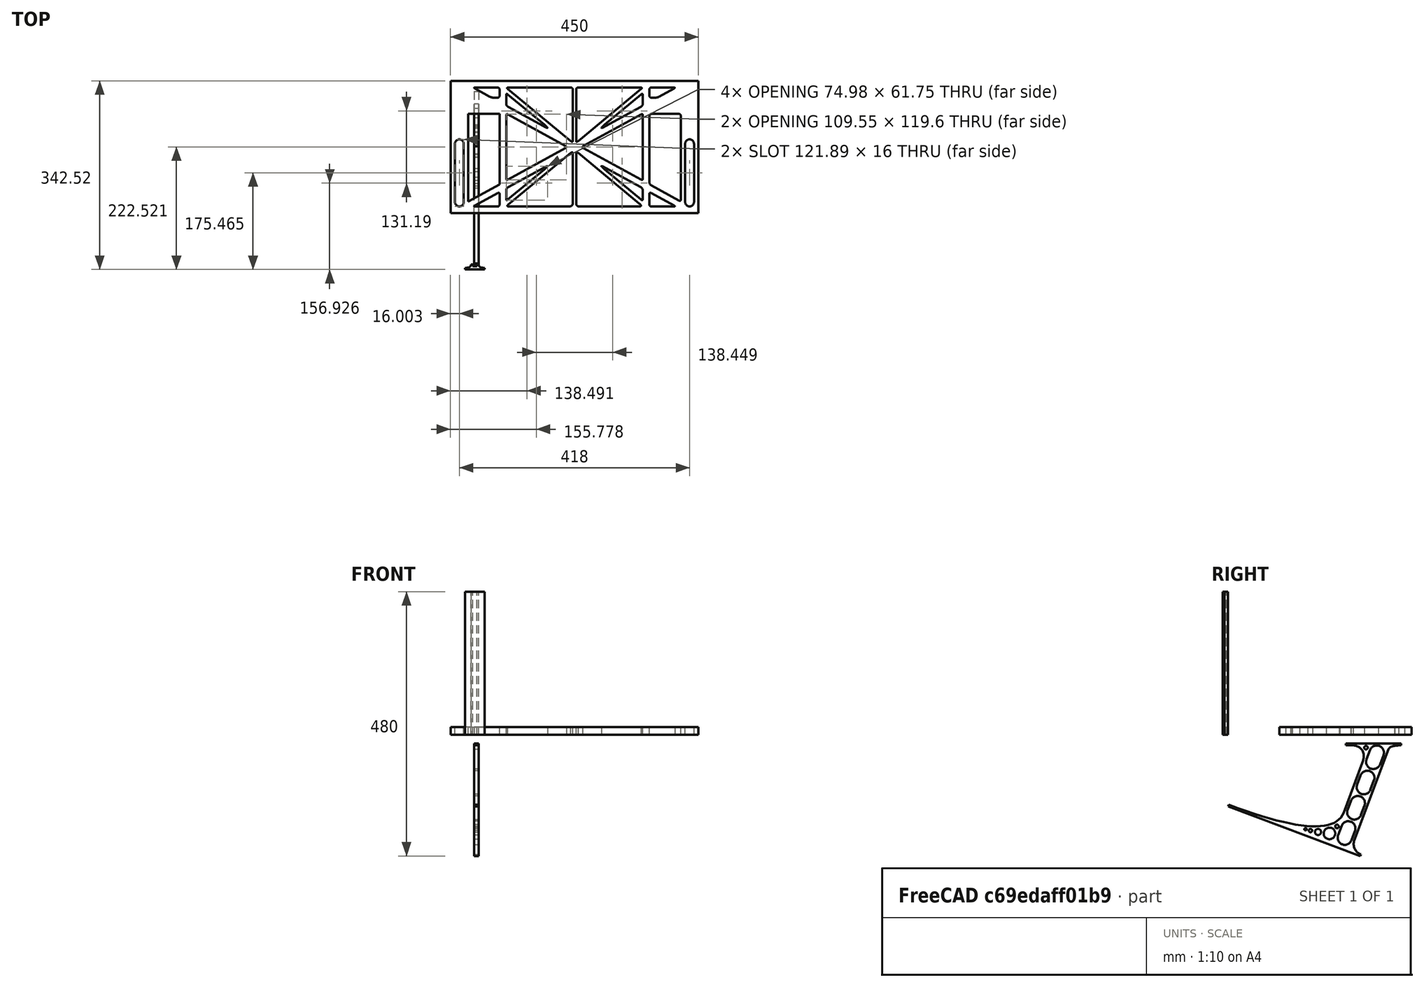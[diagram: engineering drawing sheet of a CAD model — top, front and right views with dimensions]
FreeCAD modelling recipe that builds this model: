
FCSTD DOCUMENT  (FreeCAD 0.19R0.19.2)
Label: laptopStand148FCStd
License: All rights reserved
LicenseURL: http://en.wikipedia.org/wiki/All_rights_reserved
objects: Sketcher::SketchObject×4, Part::Extrusion×3
note: 7 computed .brp shape members not serialized (recipe doc carries the construction recipe); baked Part::Feature solids carry a one-line shape summary decoded from their .brp

FEATURE [Sketcher::SketchObject] Sketch
  FullyConstrained = false
  sketch-geometry (349):
    g0: LineSegment StartX=-10.9272 StartY=-82.7794 StartZ=0 EndX=46.0728 EndY=-51.4823 EndZ=0
    g1: LineSegment StartX=-10.9272 StartY=76.4095 StartZ=0 EndX=-10.9272 EndY=-82.7794 EndZ=0
    g2: LineSegment StartX=46.0728 StartY=76.4095 StartZ=0 EndX=46.0728 EndY=-51.4823 EndZ=0
    g3: LineSegment StartX=-42.9272 StartY=136.221 StartZ=0 EndX=-42.9272 EndY=-103.779 EndZ=0
    g4: LineSegment StartX=407.073 StartY=136.221 StartZ=0 EndX=407.073 EndY=-103.779 EndZ=0
    g5: ArcOfCircle CenterX=-26.9272 CenterY=-83.7794 CenterZ=0 NormalX=0 NormalY=0 NormalZ=1 AngleXU=0 Radius=8 StartAngle=3.14159 EndAngle=6.28319
    g6: ArcOfCircle CenterX=391.073 CenterY=22.1087 CenterZ=0 NormalX=0 NormalY=0 NormalZ=1 AngleXU=0 Radius=8 StartAngle=-4.4e-15 EndAngle=3.14159
    g7: LineSegment StartX=399.073 StartY=22.1087 StartZ=0 EndX=399.073 EndY=-83.7794 EndZ=0
    g8: LineSegment StartX=383.073 StartY=22.1087 StartZ=0 EndX=383.073 EndY=-83.7794 EndZ=0
    g9: ArcOfCircle CenterX=391.073 CenterY=-83.7794 CenterZ=0 NormalX=0 NormalY=0 NormalZ=1 AngleXU=0 Radius=8 StartAngle=3.14159 EndAngle=6.28319
    g10: Circle CenterX=175.022 CenterY=27.0628 CenterZ=0 NormalX=0 NormalY=0 NormalZ=1 AngleXU=0 Radius=1
    g11: Circle CenterX=179.022 CenterY=24.8665 CenterZ=0 NormalX=0 NormalY=0 NormalZ=1 AngleXU=0 Radius=1
    g12: Circle CenterX=179.022 CenterY=27.0628 CenterZ=0 NormalX=0 NormalY=0 NormalZ=1 AngleXU=0 Radius=1
    g13: BSplineCurve PolesCount=3 KnotsCount=2 Degree=2 IsPeriodic=0
    g14: GeomPoint X=175.022 Y=27.0628 Z=0
    g15: GeomPoint X=179.022 Y=27.0628 Z=0
    g16: Circle CenterX=189.124 CenterY=27.0628 CenterZ=0 NormalX=0 NormalY=0 NormalZ=1 AngleXU=0 Radius=1
    g17: Circle CenterX=185.124 CenterY=24.8665 CenterZ=0 NormalX=0 NormalY=0 NormalZ=1 AngleXU=0 Radius=1
    g18: Circle CenterX=185.124 CenterY=27.0628 CenterZ=0 NormalX=0 NormalY=0 NormalZ=1 AngleXU=0 Radius=1
    g19: BSplineCurve PolesCount=3 KnotsCount=2 Degree=2 IsPeriodic=0
    g20: GeomPoint X=189.124 Y=27.0628 Z=0
    g21: GeomPoint X=185.124 Y=27.0628 Z=0
    g22: Circle CenterX=175.022 CenterY=5.37834 CenterZ=0 NormalX=0 NormalY=0 NormalZ=1 AngleXU=0 Radius=1
    g23: Circle CenterX=179.022 CenterY=7.57463 CenterZ=0 NormalX=0 NormalY=0 NormalZ=1 AngleXU=0 Radius=1
    g24: Circle CenterX=179.022 CenterY=5.34704 CenterZ=0 NormalX=0 NormalY=0 NormalZ=1 AngleXU=0 Radius=1
    g25: BSplineCurve PolesCount=3 KnotsCount=2 Degree=2 IsPeriodic=0
    g26: GeomPoint X=175.022 Y=5.37834 Z=0
    g27: GeomPoint X=179.022 Y=5.34704 Z=0
    g28: Circle CenterX=189.124 CenterY=5.37834 CenterZ=0 NormalX=0 NormalY=0 NormalZ=1 AngleXU=0 Radius=1
    g29: Circle CenterX=185.124 CenterY=7.57463 CenterZ=0 NormalX=0 NormalY=0 NormalZ=1 AngleXU=0 Radius=1
    g30: Circle CenterX=185.124 CenterY=5.34704 CenterZ=0 NormalX=0 NormalY=0 NormalZ=1 AngleXU=0 Radius=1
    g31: BSplineCurve PolesCount=3 KnotsCount=2 Degree=2 IsPeriodic=0
    g32: GeomPoint X=189.124 Y=5.37834 Z=0
    g33: GeomPoint X=185.124 Y=5.34704 Z=0
    g34: Circle CenterX=165.871 CenterY=18.1458 CenterZ=0 NormalX=0 NormalY=0 NormalZ=1 AngleXU=0 Radius=1
    g35: Circle CenterX=169.377 CenterY=16.2206 CenterZ=0 NormalX=0 NormalY=0 NormalZ=1 AngleXU=0 Radius=1
    g36: Circle CenterX=165.871 CenterY=14.2954 CenterZ=0 NormalX=0 NormalY=0 NormalZ=1 AngleXU=0 Radius=1
    g37: BSplineCurve PolesCount=3 KnotsCount=2 Degree=2 IsPeriodic=0
    g38: GeomPoint X=165.871 Y=18.1458 Z=0
    g39: GeomPoint X=165.871 Y=14.2954 Z=0
    g40: Circle CenterX=198.275 CenterY=18.1458 CenterZ=0 NormalX=0 NormalY=0 NormalZ=1 AngleXU=0 Radius=1
    g41: Circle CenterX=194.768 CenterY=16.2206 CenterZ=0 NormalX=0 NormalY=0 NormalZ=1 AngleXU=0 Radius=1
    g42: Circle CenterX=198.275 CenterY=14.2954 CenterZ=0 NormalX=0 NormalY=0 NormalZ=1 AngleXU=0 Radius=1
    g43: BSplineCurve PolesCount=3 KnotsCount=2 Degree=2 IsPeriodic=0
    g44: GeomPoint X=198.275 Y=18.1458 Z=0
    g45: GeomPoint X=198.275 Y=14.2954 Z=0
    g46: LineSegment StartX=407.073 StartY=-103.779 StartZ=0 EndX=-42.9272 EndY=-103.779 EndZ=0
    g47: LineSegment StartX=407.073 StartY=136.221 StartZ=0 EndX=-42.9272 EndY=136.221 EndZ=0
    g48: LineSegment StartX=46.0728 StartY=76.4095 StartZ=0 EndX=-10.9272 EndY=76.4095 EndZ=0
    g49: Circle CenterX=125.607 CenterY=54.1951 CenterZ=0 NormalX=0 NormalY=0 NormalZ=1 AngleXU=0 Radius=1
    g50: Circle CenterX=139.632 CenterY=46.4944 CenterZ=0 NormalX=0 NormalY=0 NormalZ=1 AngleXU=0 Radius=1
    g51: Circle CenterX=127.326 CenterY=56.7187 CenterZ=0 NormalX=0 NormalY=0 NormalZ=1 AngleXU=0 Radius=1
    g52: BSplineCurve PolesCount=3 KnotsCount=2 Degree=2 IsPeriodic=0
    g53: GeomPoint X=125.607 Y=54.1951 Z=0
    g54: GeomPoint X=127.326 Y=56.7187 Z=0
    g55: Circle CenterX=236.821 CenterY=56.7187 CenterZ=0 NormalX=0 NormalY=0 NormalZ=1 AngleXU=0 Radius=1
    g56: Circle CenterX=224.513 CenterY=46.4944 CenterZ=0 NormalX=0 NormalY=0 NormalZ=1 AngleXU=0 Radius=1
    g57: Circle CenterX=238.538 CenterY=54.1951 CenterZ=0 NormalX=0 NormalY=0 NormalZ=1 AngleXU=0 Radius=1
    g58: BSplineCurve PolesCount=3 KnotsCount=2 Degree=2 IsPeriodic=0
    g59: GeomPoint X=236.821 Y=56.7187 Z=0
    g60: GeomPoint X=238.538 Y=54.1951 Z=0
    g61: Circle CenterX=238.538 CenterY=-21.7539 CenterZ=0 NormalX=0 NormalY=0 NormalZ=1 AngleXU=0 Radius=1
    g62: Circle CenterX=224.513 CenterY=-14.0532 CenterZ=0 NormalX=0 NormalY=0 NormalZ=1 AngleXU=0 Radius=1
    g63: Circle CenterX=236.821 CenterY=-24.2775 CenterZ=0 NormalX=0 NormalY=0 NormalZ=1 AngleXU=0 Radius=1
    g64: BSplineCurve PolesCount=3 KnotsCount=2 Degree=2 IsPeriodic=0
    g65: GeomPoint X=238.538 Y=-21.7539 Z=0
    g66: GeomPoint X=236.821 Y=-24.2775 Z=0
    g67: Circle CenterX=125.607 CenterY=-21.7539 CenterZ=0 NormalX=0 NormalY=0 NormalZ=1 AngleXU=0 Radius=1
    g68: Circle CenterX=139.632 CenterY=-14.0532 CenterZ=0 NormalX=0 NormalY=0 NormalZ=1 AngleXU=0 Radius=1
    g69: Circle CenterX=127.325 CenterY=-24.2775 CenterZ=0 NormalX=0 NormalY=0 NormalZ=1 AngleXU=0 Radius=1
    g70: BSplineCurve PolesCount=3 KnotsCount=2 Degree=2 IsPeriodic=0
    g71: GeomPoint X=125.607 Y=-21.7539 Z=0
    g72: GeomPoint X=127.325 Y=-24.2775 Z=0
    g73: Circle CenterX=302.996 CenterY=111.695 CenterZ=0 NormalX=0 NormalY=0 NormalZ=1 AngleXU=0 Radius=1
    g74: Circle CenterX=306.073 CenterY=114.251 CenterZ=0 NormalX=0 NormalY=0 NormalZ=1 AngleXU=0 Radius=1
    g75: Circle CenterX=306.073 CenterY=110.251 CenterZ=0 NormalX=0 NormalY=0 NormalZ=1 AngleXU=0 Radius=1
    g76: BSplineCurve PolesCount=3 KnotsCount=2 Degree=2 IsPeriodic=0
    g77: GeomPoint X=302.996 Y=111.695 Z=0
    g78: GeomPoint X=306.073 Y=110.251 Z=0
    g79: Circle CenterX=306.073 CenterY=95.2763 CenterZ=0 NormalX=0 NormalY=0 NormalZ=1 AngleXU=0 Radius=1
    g80: Circle CenterX=306.073 CenterY=91.2763 CenterZ=0 NormalX=0 NormalY=0 NormalZ=1 AngleXU=0 Radius=1
    g81: Circle CenterX=302.567 CenterY=89.3511 CenterZ=0 NormalX=0 NormalY=0 NormalZ=1 AngleXU=0 Radius=1
    g82: BSplineCurve PolesCount=3 KnotsCount=2 Degree=2 IsPeriodic=0
    g83: GeomPoint X=306.073 Y=95.2763 Z=0
    g84: GeomPoint X=302.567 Y=89.3511 Z=0
    g85: LineSegment StartX=306.073 StartY=110.251 StartZ=0 EndX=306.073 EndY=95.2763 EndZ=0
    g86: LineSegment StartX=302.996 StartY=111.695 StartZ=0 EndX=236.821 EndY=56.7187 EndZ=0
    g87: LineSegment StartX=238.538 StartY=54.1951 StartZ=0 EndX=302.567 EndY=89.3511 EndZ=0
    g88: Circle CenterX=61.1496 CenterY=111.695 CenterZ=0 NormalX=0 NormalY=0 NormalZ=1 AngleXU=0 Radius=1
    g89: Circle CenterX=58.0728 CenterY=114.251 CenterZ=0 NormalX=0 NormalY=0 NormalZ=1 AngleXU=0 Radius=1
    g90: Circle CenterX=58.0728 CenterY=110.251 CenterZ=0 NormalX=0 NormalY=0 NormalZ=1 AngleXU=0 Radius=1
    g91: BSplineCurve PolesCount=3 KnotsCount=2 Degree=2 IsPeriodic=0
    g92: GeomPoint X=61.1496 Y=111.695 Z=0
    g93: GeomPoint X=58.0728 Y=110.251 Z=0
    g94: Circle CenterX=61.5791 CenterY=89.3511 CenterZ=0 NormalX=0 NormalY=0 NormalZ=1 AngleXU=0 Radius=1
    g95: Circle CenterX=58.0728 CenterY=91.2763 CenterZ=0 NormalX=0 NormalY=0 NormalZ=1 AngleXU=0 Radius=1
    g96: Circle CenterX=58.0728 CenterY=95.2763 CenterZ=0 NormalX=0 NormalY=0 NormalZ=1 AngleXU=0 Radius=1
    g97: BSplineCurve PolesCount=3 KnotsCount=2 Degree=2 IsPeriodic=0
    g98: GeomPoint X=61.5791 Y=89.3511 Z=0
    g99: GeomPoint X=58.0728 Y=95.2763 Z=0
    g100: LineSegment StartX=58.0728 StartY=110.251 StartZ=0 EndX=58.0728 EndY=95.2763 EndZ=0
    g101: LineSegment StartX=61.1496 StartY=111.695 StartZ=0 EndX=127.326 EndY=56.7187 EndZ=0
    g102: LineSegment StartX=125.607 StartY=54.1951 StartZ=0 EndX=61.5791 EndY=89.3511 EndZ=0
    g103: Circle CenterX=61.5791 CenterY=-56.9099 CenterZ=0 NormalX=0 NormalY=0 NormalZ=1 AngleXU=0 Radius=1
    g104: Circle CenterX=58.0728 CenterY=-58.8351 CenterZ=0 NormalX=0 NormalY=0 NormalZ=1 AngleXU=0 Radius=1
    g105: Circle CenterX=58.0728 CenterY=-62.8351 CenterZ=0 NormalX=0 NormalY=0 NormalZ=1 AngleXU=0 Radius=1
    g106: BSplineCurve PolesCount=3 KnotsCount=2 Degree=2 IsPeriodic=0
    g107: GeomPoint X=61.5791 Y=-56.9099 Z=0
    g108: GeomPoint X=58.0728 Y=-62.8351 Z=0
    g109: Circle CenterX=58.0728 CenterY=-77.8102 CenterZ=0 NormalX=0 NormalY=0 NormalZ=1 AngleXU=0 Radius=1
    g110: Circle CenterX=58.0728 CenterY=-81.8102 CenterZ=0 NormalX=0 NormalY=0 NormalZ=1 AngleXU=0 Radius=1
    g111: Circle CenterX=61.1496 CenterY=-79.2541 CenterZ=0 NormalX=0 NormalY=0 NormalZ=1 AngleXU=0 Radius=1
    g112: BSplineCurve PolesCount=3 KnotsCount=2 Degree=2 IsPeriodic=0
    g113: GeomPoint X=58.0728 Y=-77.8102 Z=0
    g114: GeomPoint X=61.1496 Y=-79.2541 Z=0
    g115: LineSegment StartX=58.0728 StartY=-62.8351 StartZ=0 EndX=58.0728 EndY=-77.8102 EndZ=0
    g116: LineSegment StartX=61.1496 StartY=-79.2541 StartZ=0 EndX=127.325 EndY=-24.2775 EndZ=0
    g117: LineSegment StartX=125.607 StartY=-21.7539 StartZ=0 EndX=61.5791 EndY=-56.9099 EndZ=0
    g118: Circle CenterX=302.567 CenterY=-56.9099 CenterZ=0 NormalX=0 NormalY=0 NormalZ=1 AngleXU=0 Radius=1
    g119: Circle CenterX=306.073 CenterY=-58.8351 CenterZ=0 NormalX=0 NormalY=0 NormalZ=1 AngleXU=0 Radius=1
    g120: Circle CenterX=306.073 CenterY=-62.8351 CenterZ=0 NormalX=0 NormalY=0 NormalZ=1 AngleXU=0 Radius=1
    g121: BSplineCurve PolesCount=3 KnotsCount=2 Degree=2 IsPeriodic=0
    g122: GeomPoint X=302.567 Y=-56.9099 Z=0
    g123: GeomPoint X=306.073 Y=-62.8351 Z=0
    g124: Circle CenterX=302.996 CenterY=-79.2541 CenterZ=0 NormalX=0 NormalY=0 NormalZ=1 AngleXU=0 Radius=1
    g125: Circle CenterX=306.073 CenterY=-81.8102 CenterZ=0 NormalX=0 NormalY=0 NormalZ=1 AngleXU=0 Radius=1
    g126: Circle CenterX=306.073 CenterY=-77.8102 CenterZ=0 NormalX=0 NormalY=0 NormalZ=1 AngleXU=0 Radius=1
    g127: BSplineCurve PolesCount=3 KnotsCount=2 Degree=2 IsPeriodic=0
    g128: GeomPoint X=302.996 Y=-79.2541 Z=0
    g129: GeomPoint X=306.073 Y=-77.8102 Z=0
    g130: LineSegment StartX=306.073 StartY=-62.8351 StartZ=0 EndX=306.073 EndY=-77.8102 EndZ=0
    g131: LineSegment StartX=302.996 StartY=-79.2541 StartZ=0 EndX=236.821 EndY=-24.2775 EndZ=0
    g132: LineSegment StartX=238.538 StartY=-21.7539 StartZ=0 EndX=302.567 EndY=-56.9099 EndZ=0
    g133: Circle CenterX=61.6457 CenterY=-88.8112 CenterZ=0 NormalX=0 NormalY=0 NormalZ=1 AngleXU=0 Radius=1
    g134: Circle CenterX=58.0728 CenterY=-91.7794 CenterZ=0 NormalX=0 NormalY=0 NormalZ=1 AngleXU=0 Radius=1
    g135: Circle CenterX=63.9135 CenterY=-91.7794 CenterZ=0 NormalX=0 NormalY=0 NormalZ=1 AngleXU=0 Radius=1
    g136: BSplineCurve PolesCount=3 KnotsCount=2 Degree=2 IsPeriodic=0
    g137: GeomPoint X=61.6457 Y=-88.8112 Z=0
    g138: GeomPoint X=63.9135 Y=-91.7794 Z=0
    g139: Circle CenterX=179.022 CenterY=-85.8163 CenterZ=0 NormalX=0 NormalY=0 NormalZ=1 AngleXU=0 Radius=1
    g140: Circle CenterX=179.022 CenterY=-91.7794 CenterZ=0 NormalX=0 NormalY=0 NormalZ=1 AngleXU=0 Radius=1
    g141: Circle CenterX=171.895 CenterY=-91.7794 CenterZ=0 NormalX=0 NormalY=0 NormalZ=1 AngleXU=0 Radius=1
    g142: BSplineCurve PolesCount=3 KnotsCount=2 Degree=2 IsPeriodic=0
    g143: GeomPoint X=179.022 Y=-85.8163 Z=0
    g144: GeomPoint X=171.895 Y=-91.7794 Z=0
    g145: Circle CenterX=185.124 CenterY=-86.2028 CenterZ=0 NormalX=0 NormalY=0 NormalZ=1 AngleXU=0 Radius=1
    g146: Circle CenterX=185.124 CenterY=-91.7794 CenterZ=0 NormalX=0 NormalY=0 NormalZ=1 AngleXU=0 Radius=1
    g147: Circle CenterX=191.747 CenterY=-91.7794 CenterZ=0 NormalX=0 NormalY=0 NormalZ=1 AngleXU=0 Radius=1
    g148: BSplineCurve PolesCount=3 KnotsCount=2 Degree=2 IsPeriodic=0
    g149: GeomPoint X=185.124 Y=-86.2028 Z=0
    g150: GeomPoint X=191.747 Y=-91.7794 Z=0
    g151: Circle CenterX=299.888 CenterY=-86.6413 CenterZ=0 NormalX=0 NormalY=0 NormalZ=1 AngleXU=0 Radius=1
    g152: Circle CenterX=306.073 CenterY=-91.7794 CenterZ=0 NormalX=0 NormalY=0 NormalZ=1 AngleXU=0 Radius=1
    g153: Circle CenterX=298.776 CenterY=-91.7794 CenterZ=0 NormalX=0 NormalY=0 NormalZ=1 AngleXU=0 Radius=1
    g154: BSplineCurve PolesCount=3 KnotsCount=2 Degree=2 IsPeriodic=0
    g155: GeomPoint X=299.888 Y=-86.6413 Z=0
    g156: GeomPoint X=298.776 Y=-91.7794 Z=0
    g157: LineSegment StartX=189.124 StartY=5.37834 StartZ=0 EndX=299.888 EndY=-86.6413 EndZ=0
    g158: LineSegment StartX=298.776 StartY=-91.7794 StartZ=0 EndX=191.747 EndY=-91.7794 EndZ=0
    g159: LineSegment StartX=185.124 StartY=-86.2028 StartZ=0 EndX=185.124 EndY=5.34704 EndZ=0
    g160: LineSegment StartX=179.022 StartY=5.34704 StartZ=0 EndX=179.022 EndY=-85.8163 EndZ=0
    g161: LineSegment StartX=171.895 StartY=-91.7794 StartZ=0 EndX=63.9135 EndY=-91.7794 EndZ=0
    g162: LineSegment StartX=61.6457 StartY=-88.8112 StartZ=0 EndX=175.022 EndY=5.37834 EndZ=0
    g163: Circle CenterX=302.073 CenterY=124.221 CenterZ=0 NormalX=0 NormalY=0 NormalZ=1 AngleXU=0 Radius=1
    g164: Circle CenterX=306.073 CenterY=124.221 CenterZ=0 NormalX=0 NormalY=0 NormalZ=1 AngleXU=0 Radius=1
    g165: Circle CenterX=302.996 CenterY=121.665 CenterZ=0 NormalX=0 NormalY=0 NormalZ=1 AngleXU=0 Radius=1
    g166: BSplineCurve PolesCount=3 KnotsCount=2 Degree=2 IsPeriodic=0
    g167: GeomPoint X=302.073 Y=124.221 Z=0
    g168: GeomPoint X=302.996 Y=121.665 Z=0
    g169: Circle CenterX=189.124 CenterY=124.221 CenterZ=0 NormalX=0 NormalY=0 NormalZ=1 AngleXU=0 Radius=1
    g170: Circle CenterX=185.124 CenterY=124.221 CenterZ=0 NormalX=0 NormalY=0 NormalZ=1 AngleXU=0 Radius=1
    g171: Circle CenterX=185.124 CenterY=120.221 CenterZ=0 NormalX=0 NormalY=0 NormalZ=1 AngleXU=0 Radius=1
    g172: BSplineCurve PolesCount=3 KnotsCount=2 Degree=2 IsPeriodic=0
    g173: GeomPoint X=189.124 Y=124.221 Z=0
    g174: GeomPoint X=185.124 Y=120.221 Z=0
    g175: Circle CenterX=175.022 CenterY=124.221 CenterZ=0 NormalX=0 NormalY=0 NormalZ=1 AngleXU=0 Radius=1
    g176: Circle CenterX=179.022 CenterY=124.221 CenterZ=0 NormalX=0 NormalY=0 NormalZ=1 AngleXU=0 Radius=1
    g177: Circle CenterX=179.022 CenterY=120.221 CenterZ=0 NormalX=0 NormalY=0 NormalZ=1 AngleXU=0 Radius=1
    g178: BSplineCurve PolesCount=3 KnotsCount=2 Degree=2 IsPeriodic=0
    g179: GeomPoint X=175.022 Y=124.221 Z=0
    g180: GeomPoint X=179.022 Y=120.221 Z=0
    g181: Circle CenterX=62.0728 CenterY=124.221 CenterZ=0 NormalX=0 NormalY=0 NormalZ=1 AngleXU=0 Radius=1
    g182: Circle CenterX=58.0728 CenterY=124.221 CenterZ=0 NormalX=0 NormalY=0 NormalZ=1 AngleXU=0 Radius=1
    g183: Circle CenterX=61.1496 CenterY=121.665 CenterZ=0 NormalX=0 NormalY=0 NormalZ=1 AngleXU=0 Radius=1
    g184: BSplineCurve PolesCount=3 KnotsCount=2 Degree=2 IsPeriodic=0
    g185: GeomPoint X=62.0728 Y=124.221 Z=0
    g186: GeomPoint X=61.1496 Y=121.665 Z=0
    g187: LineSegment StartX=62.0728 StartY=124.221 StartZ=0 EndX=175.022 EndY=124.221 EndZ=0
    g188: LineSegment StartX=179.022 StartY=120.221 StartZ=0 EndX=179.022 EndY=27.0628 EndZ=0
    g189: LineSegment StartX=185.124 StartY=27.0628 StartZ=0 EndX=185.124 EndY=120.221 EndZ=0
    g190: LineSegment StartX=189.124 StartY=124.221 StartZ=0 EndX=302.073 EndY=124.221 EndZ=0
    g191: LineSegment StartX=302.996 StartY=121.665 StartZ=0 EndX=189.124 EndY=27.0628 EndZ=0
    g192: LineSegment StartX=175.022 StartY=27.0628 StartZ=0 EndX=61.1496 EndY=121.665 EndZ=0
    g193: Circle CenterX=61.5791 CenterY=75.4095 CenterZ=0 NormalX=0 NormalY=0 NormalZ=1 AngleXU=0 Radius=1
    g194: Circle CenterX=58.0728 CenterY=77.3346 CenterZ=0 NormalX=0 NormalY=0 NormalZ=1 AngleXU=0 Radius=1
    g195: Circle CenterX=58.0728 CenterY=73.3346 CenterZ=0 NormalX=0 NormalY=0 NormalZ=1 AngleXU=0 Radius=1
    g196: BSplineCurve PolesCount=3 KnotsCount=2 Degree=2 IsPeriodic=0
    g197: GeomPoint X=61.5791 Y=75.4095 Z=0
    g198: GeomPoint X=58.0728 Y=73.3346 Z=0
    g199: Circle CenterX=58.0728 CenterY=-40.8935 CenterZ=0 NormalX=0 NormalY=0 NormalZ=1 AngleXU=0 Radius=1
    g200: Circle CenterX=58.0728 CenterY=-44.8935 CenterZ=0 NormalX=0 NormalY=0 NormalZ=1 AngleXU=0 Radius=1
    g201: Circle CenterX=61.5791 CenterY=-42.9683 CenterZ=0 NormalX=0 NormalY=0 NormalZ=1 AngleXU=0 Radius=1
    g202: BSplineCurve PolesCount=3 KnotsCount=2 Degree=2 IsPeriodic=0
    g203: GeomPoint X=58.0728 Y=-40.8935 Z=0
    g204: GeomPoint X=61.5791 Y=-42.9683 Z=0
    g205: LineSegment StartX=61.5791 StartY=-42.9683 StartZ=0 EndX=165.871 EndY=14.2954 EndZ=0
    g206: LineSegment StartX=165.871 StartY=18.1458 StartZ=0 EndX=61.5791 EndY=75.4095 EndZ=0
    g207: LineSegment StartX=58.0728 StartY=73.3346 StartZ=0 EndX=58.0728 EndY=-40.8935 EndZ=0
    g208: Circle CenterX=302.567 CenterY=-42.9683 CenterZ=0 NormalX=0 NormalY=0 NormalZ=1 AngleXU=0 Radius=1
    g209: Circle CenterX=306.073 CenterY=-44.8935 CenterZ=0 NormalX=0 NormalY=0 NormalZ=1 AngleXU=0 Radius=1
    g210: Circle CenterX=306.073 CenterY=-40.8935 CenterZ=0 NormalX=0 NormalY=0 NormalZ=1 AngleXU=0 Radius=1
    g211: BSplineCurve PolesCount=3 KnotsCount=2 Degree=2 IsPeriodic=0
    g212: GeomPoint X=302.567 Y=-42.9683 Z=0
    g213: GeomPoint X=306.073 Y=-40.8935 Z=0
    g214: Circle CenterX=306.073 CenterY=73.3346 CenterZ=0 NormalX=0 NormalY=0 NormalZ=1 AngleXU=0 Radius=1
    g215: Circle CenterX=306.073 CenterY=77.3346 CenterZ=0 NormalX=0 NormalY=0 NormalZ=1 AngleXU=0 Radius=1
    g216: Circle CenterX=302.567 CenterY=75.4095 CenterZ=0 NormalX=0 NormalY=0 NormalZ=1 AngleXU=0 Radius=1
    g217: BSplineCurve PolesCount=3 KnotsCount=2 Degree=2 IsPeriodic=0
    g218: GeomPoint X=306.073 Y=73.3346 Z=0
    g219: GeomPoint X=302.567 Y=75.4095 Z=0
    g220: LineSegment StartX=302.567 StartY=-42.9683 StartZ=0 EndX=198.275 EndY=14.2954 EndZ=0
    g221: LineSegment StartX=198.275 StartY=18.1458 StartZ=0 EndX=302.567 EndY=75.4095 EndZ=0
    g222: LineSegment StartX=306.073 StartY=73.3346 StartZ=0 EndX=306.073 EndY=-40.8935 EndZ=0
    g223: LineSegment StartX=322.073 StartY=105.865 StartZ=0 EndX=328.643 EndY=105.865 EndZ=0
    g224: LineSegment StartX=318.073 StartY=120.221 StartZ=0 EndX=318.073 EndY=109.865 EndZ=0
    g225: LineSegment StartX=336.157 StartY=107.779 StartZ=0 EndX=362.567 EndY=122.294 EndZ=0
    g226: Circle CenterX=362.073 CenterY=124.221 CenterZ=0 NormalX=0 NormalY=0 NormalZ=1 AngleXU=0 Radius=1
    g227: Circle CenterX=366.073 CenterY=124.221 CenterZ=0 NormalX=0 NormalY=0 NormalZ=1 AngleXU=0 Radius=1
    g228: Circle CenterX=362.567 CenterY=122.294 CenterZ=0 NormalX=0 NormalY=0 NormalZ=1 AngleXU=0 Radius=1
    g229: BSplineCurve PolesCount=3 KnotsCount=2 Degree=2 IsPeriodic=0
    g230: GeomPoint X=362.073 Y=124.221 Z=0
    g231: GeomPoint X=362.567 Y=122.294 Z=0
    g232: Circle CenterX=322.073 CenterY=124.221 CenterZ=0 NormalX=0 NormalY=0 NormalZ=1 AngleXU=0 Radius=1
    g233: Circle CenterX=318.073 CenterY=124.221 CenterZ=0 NormalX=0 NormalY=0 NormalZ=1 AngleXU=0 Radius=1
    g234: Circle CenterX=318.073 CenterY=120.221 CenterZ=0 NormalX=0 NormalY=0 NormalZ=1 AngleXU=0 Radius=1
    g235: BSplineCurve PolesCount=3 KnotsCount=2 Degree=2 IsPeriodic=0
    g236: GeomPoint X=322.073 Y=124.221 Z=0
    g237: GeomPoint X=318.073 Y=120.221 Z=0
    g238: Circle CenterX=322.073 CenterY=105.865 CenterZ=0 NormalX=0 NormalY=0 NormalZ=1 AngleXU=0 Radius=1
    g239: Circle CenterX=318.073 CenterY=105.865 CenterZ=0 NormalX=0 NormalY=0 NormalZ=1 AngleXU=0 Radius=1
    g240: Circle CenterX=318.073 CenterY=109.865 CenterZ=0 NormalX=0 NormalY=0 NormalZ=1 AngleXU=0 Radius=1
    g241: BSplineCurve PolesCount=3 KnotsCount=2 Degree=2 IsPeriodic=0
    g242: GeomPoint X=322.073 Y=105.865 Z=0
    g243: GeomPoint X=318.073 Y=109.865 Z=0
    g244: Circle CenterX=336.157 CenterY=107.779 CenterZ=0 NormalX=0 NormalY=0 NormalZ=1 AngleXU=0 Radius=1
    g245: Circle CenterX=332.651 CenterY=105.853 CenterZ=0 NormalX=0 NormalY=0 NormalZ=1 AngleXU=0 Radius=1
    g246: Circle CenterX=328.643 CenterY=105.865 CenterZ=0 NormalX=0 NormalY=0 NormalZ=1 AngleXU=0 Radius=1
    g247: BSplineCurve PolesCount=3 KnotsCount=2 Degree=2 IsPeriodic=0
    g248: GeomPoint X=336.157 Y=107.779 Z=0
    g249: GeomPoint X=328.643 Y=105.865 Z=0
    g250: LineSegment StartX=322.073 StartY=124.221 StartZ=0 EndX=362.073 EndY=124.221 EndZ=0
    g251: Circle CenterX=371.567 CenterY=-80.8644 CenterZ=0 NormalX=0 NormalY=0 NormalZ=1 AngleXU=0 Radius=1
    g252: Circle CenterX=375.073 CenterY=-82.7896 CenterZ=0 NormalX=0 NormalY=0 NormalZ=1 AngleXU=0 Radius=1
    g253: Circle CenterX=375.073 CenterY=-78.7896 CenterZ=0 NormalX=0 NormalY=0 NormalZ=1 AngleXU=0 Radius=1
    g254: BSplineCurve PolesCount=3 KnotsCount=2 Degree=2 IsPeriodic=0
    g255: GeomPoint X=371.567 Y=-80.8644 Z=0
    g256: GeomPoint X=375.073 Y=-78.7896 Z=0
    g257: Circle CenterX=321.579 CenterY=-53.4075 CenterZ=0 NormalX=0 NormalY=0 NormalZ=1 AngleXU=0 Radius=1
    g258: Circle CenterX=318.073 CenterY=-51.4823 CenterZ=0 NormalX=0 NormalY=0 NormalZ=1 AngleXU=0 Radius=1
    g259: Circle CenterX=318.073 CenterY=-47.4805 CenterZ=0 NormalX=0 NormalY=0 NormalZ=1 AngleXU=0 Radius=1
    g260: BSplineCurve PolesCount=3 KnotsCount=2 Degree=2 IsPeriodic=0
    g261: GeomPoint X=321.579 Y=-53.4075 Z=0
    g262: GeomPoint X=318.073 Y=-47.4805 Z=0
    g263: LineSegment StartX=371.567 StartY=-80.8644 StartZ=0 EndX=321.579 EndY=-53.4075 EndZ=0
    g264: Circle CenterX=321.579 CenterY=-67.3492 CenterZ=0 NormalX=0 NormalY=0 NormalZ=1 AngleXU=0 Radius=1
    g265: Circle CenterX=318.073 CenterY=-65.424 CenterZ=0 NormalX=0 NormalY=0 NormalZ=1 AngleXU=0 Radius=1
    g266: Circle CenterX=318.073 CenterY=-69.424 CenterZ=0 NormalX=0 NormalY=0 NormalZ=1 AngleXU=0 Radius=1
    g267: BSplineCurve PolesCount=3 KnotsCount=2 Degree=2 IsPeriodic=0
    g268: GeomPoint X=321.579 Y=-67.3492 Z=0
    g269: GeomPoint X=318.073 Y=-69.424 Z=0
    g270: Circle CenterX=362.567 CenterY=-89.8542 CenterZ=0 NormalX=0 NormalY=0 NormalZ=1 AngleXU=0 Radius=1
    g271: Circle CenterX=366.073 CenterY=-91.7794 CenterZ=0 NormalX=0 NormalY=0 NormalZ=1 AngleXU=0 Radius=1
    g272: Circle CenterX=362.073 CenterY=-91.7794 CenterZ=0 NormalX=0 NormalY=0 NormalZ=1 AngleXU=0 Radius=1
    g273: BSplineCurve PolesCount=3 KnotsCount=2 Degree=2 IsPeriodic=0
    g274: GeomPoint X=362.567 Y=-89.8542 Z=0
    g275: GeomPoint X=362.073 Y=-91.7794 Z=0
    g276: Circle CenterX=322.073 CenterY=-91.7794 CenterZ=0 NormalX=0 NormalY=0 NormalZ=1 AngleXU=0 Radius=1
    g277: Circle CenterX=318.073 CenterY=-91.7794 CenterZ=0 NormalX=0 NormalY=0 NormalZ=1 AngleXU=0 Radius=1
    g278: Circle CenterX=318.073 CenterY=-87.7794 CenterZ=0 NormalX=0 NormalY=0 NormalZ=1 AngleXU=0 Radius=1
    g279: BSplineCurve PolesCount=3 KnotsCount=2 Degree=2 IsPeriodic=0
    g280: GeomPoint X=322.073 Y=-91.7794 Z=0
    g281: GeomPoint X=318.073 Y=-87.7794 Z=0
    g282: LineSegment StartX=362.567 StartY=-89.8542 StartZ=0 EndX=321.579 EndY=-67.3492 EndZ=0
    g283: LineSegment StartX=318.073 StartY=-69.424 StartZ=0 EndX=318.073 EndY=-87.7794 EndZ=0
    g284: LineSegment StartX=322.073 StartY=-91.7794 StartZ=0 EndX=362.073 EndY=-91.7794 EndZ=0
    g285: Circle CenterX=2.07281 CenterY=124.221 CenterZ=0 NormalX=0 NormalY=0 NormalZ=1 AngleXU=0 Radius=1
    g286: Circle CenterX=1.57905 CenterY=122.295 CenterZ=0 NormalX=0 NormalY=0 NormalZ=1 AngleXU=0 Radius=1
    g287: BSplineCurve PolesCount=3 KnotsCount=2 Degree=2 IsPeriodic=0
    g288: GeomPoint X=2.07281 Y=124.221 Z=0
    g289: GeomPoint X=1.57905 Y=122.295 Z=0
    g290: Circle CenterX=42.0728 CenterY=124.221 CenterZ=0 NormalX=0 NormalY=0 NormalZ=1 AngleXU=0 Radius=1
    g291: Circle CenterX=46.0728 CenterY=124.221 CenterZ=0 NormalX=0 NormalY=0 NormalZ=1 AngleXU=0 Radius=1
    g292: Circle CenterX=46.0728 CenterY=120.221 CenterZ=0 NormalX=0 NormalY=0 NormalZ=1 AngleXU=0 Radius=1
    g293: BSplineCurve PolesCount=3 KnotsCount=2 Degree=2 IsPeriodic=0
    g294: GeomPoint X=42.0728 Y=124.221 Z=0
    g295: GeomPoint X=46.0728 Y=120.221 Z=0
    g296: Circle CenterX=46.0728 CenterY=109.865 CenterZ=0 NormalX=0 NormalY=0 NormalZ=1 AngleXU=0 Radius=1
    g297: Circle CenterX=46.0728 CenterY=105.865 CenterZ=0 NormalX=0 NormalY=0 NormalZ=1 AngleXU=0 Radius=1
    g298: Circle CenterX=42.0728 CenterY=105.865 CenterZ=0 NormalX=0 NormalY=0 NormalZ=1 AngleXU=0 Radius=1
    g299: BSplineCurve PolesCount=3 KnotsCount=2 Degree=2 IsPeriodic=0
    g300: GeomPoint X=46.0728 Y=109.865 Z=0
    g301: GeomPoint X=42.0728 Y=105.865 Z=0
    g302: Circle CenterX=35.5028 CenterY=105.865 CenterZ=0 NormalX=0 NormalY=0 NormalZ=1 AngleXU=0 Radius=1
    g303: Circle CenterX=31.5028 CenterY=105.865 CenterZ=0 NormalX=0 NormalY=0 NormalZ=1 AngleXU=0 Radius=1
    g304: Circle CenterX=27.9965 CenterY=107.79 CenterZ=0 NormalX=0 NormalY=0 NormalZ=1 AngleXU=0 Radius=1
    g305: BSplineCurve PolesCount=3 KnotsCount=2 Degree=2 IsPeriodic=0
    g306: GeomPoint X=35.5028 Y=105.865 Z=0
    g307: GeomPoint X=27.9965 Y=107.79 Z=0
    g308: LineSegment StartX=2.07281 StartY=124.221 StartZ=0 EndX=42.0728 EndY=124.221 EndZ=0
    g309: LineSegment StartX=46.0728 StartY=120.221 StartZ=0 EndX=46.0728 EndY=109.865 EndZ=0
    g310: LineSegment StartX=42.0728 StartY=105.865 StartZ=0 EndX=35.5028 EndY=105.865 EndZ=0
    g311: LineSegment StartX=27.9965 StartY=107.79 StartZ=0 EndX=1.57905 EndY=122.295 EndZ=0
    g312: Circle CenterX=42.5666 CenterY=-67.3492 CenterZ=0 NormalX=0 NormalY=0 NormalZ=1 AngleXU=0 Radius=1
    g313: Circle CenterX=46.0728 CenterY=-65.424 CenterZ=0 NormalX=0 NormalY=0 NormalZ=1 AngleXU=0 Radius=1
    g314: Circle CenterX=46.0728 CenterY=-69.424 CenterZ=0 NormalX=0 NormalY=0 NormalZ=1 AngleXU=0 Radius=1
    g315: BSplineCurve PolesCount=3 KnotsCount=2 Degree=2 IsPeriodic=0
    g316: GeomPoint X=42.5666 Y=-67.3492 Z=0
    g317: GeomPoint X=46.0728 Y=-69.424 Z=0
    g318: Circle CenterX=46.0728 CenterY=-87.7794 CenterZ=0 NormalX=0 NormalY=0 NormalZ=1 AngleXU=0 Radius=1
    g319: Circle CenterX=46.0728 CenterY=-91.7794 CenterZ=0 NormalX=0 NormalY=0 NormalZ=1 AngleXU=0 Radius=1
    g320: Circle CenterX=42.0728 CenterY=-91.7794 CenterZ=0 NormalX=0 NormalY=0 NormalZ=1 AngleXU=0 Radius=1
    g321: BSplineCurve PolesCount=3 KnotsCount=2 Degree=2 IsPeriodic=0
    g322: GeomPoint X=46.0728 Y=-87.7794 Z=0
    g323: GeomPoint X=42.0728 Y=-91.7794 Z=0
    g324: Circle CenterX=2.07281 CenterY=-91.7794 CenterZ=0 NormalX=0 NormalY=0 NormalZ=1 AngleXU=0 Radius=1
    g325: Circle CenterX=-1.92719 CenterY=-91.7794 CenterZ=0 NormalX=0 NormalY=0 NormalZ=1 AngleXU=0 Radius=1
    g326: Circle CenterX=1.57905 CenterY=-89.8542 CenterZ=0 NormalX=0 NormalY=0 NormalZ=1 AngleXU=0 Radius=1
    g327: BSplineCurve PolesCount=3 KnotsCount=2 Degree=2 IsPeriodic=0
    g328: GeomPoint X=2.07281 Y=-91.7794 Z=0
    g329: GeomPoint X=1.57905 Y=-89.8542 Z=0
    g330: LineSegment StartX=2.07281 StartY=-91.7794 StartZ=0 EndX=42.0728 EndY=-91.7794 EndZ=0
    g331: LineSegment StartX=46.0728 StartY=-87.7794 StartZ=0 EndX=46.0728 EndY=-69.424 EndZ=0
    g332: LineSegment StartX=42.5666 StartY=-67.3492 StartZ=0 EndX=1.57905 EndY=-89.8542 EndZ=0
    g333: Circle CenterX=322.073 CenterY=76.4095 CenterZ=0 NormalX=0 NormalY=0 NormalZ=1 AngleXU=0 Radius=4
    g334: BSplineCurve PolesCount=3 KnotsCount=2 Degree=2 IsPeriodic=0
    g335: GeomPoint X=318.073 Y=72.4095 Z=0
    g336: GeomPoint X=322.073 Y=76.4095 Z=0
    g337: Circle CenterX=375.073 CenterY=72.4095 CenterZ=0 NormalX=0 NormalY=0 NormalZ=1 AngleXU=0 Radius=1
    g338: Circle CenterX=375.073 CenterY=76.4095 CenterZ=0 NormalX=0 NormalY=0 NormalZ=1 AngleXU=0 Radius=1
    g339: Circle CenterX=371.073 CenterY=76.4095 CenterZ=0 NormalX=0 NormalY=0 NormalZ=1 AngleXU=0 Radius=1
    g340: BSplineCurve PolesCount=3 KnotsCount=2 Degree=2 IsPeriodic=0
    g341: GeomPoint X=375.073 Y=72.4095 Z=0
    g342: GeomPoint X=371.073 Y=76.4095 Z=0
    g343: LineSegment StartX=322.073 StartY=76.4095 StartZ=0 EndX=371.073 EndY=76.4095 EndZ=0
    g344: LineSegment StartX=318.073 StartY=72.4095 StartZ=0 EndX=318.073 EndY=-47.4805 EndZ=0
    g345: LineSegment StartX=375.073 StartY=72.4095 StartZ=0 EndX=375.073 EndY=-78.7896 EndZ=0
    g346: ArcOfCircle CenterX=-26.9272 CenterY=22.1087 CenterZ=0 NormalX=0 NormalY=0 NormalZ=1 AngleXU=0 Radius=4 StartAngle=5e-16 EndAngle=3.14159
    g347: LineSegment StartX=-30.9272 StartY=22.1087 StartZ=0 EndX=-34.9272 EndY=-83.7794 EndZ=0
    g348: LineSegment StartX=-18.9272 StartY=-83.7794 StartZ=0 EndX=-22.9272 EndY=22.1087 EndZ=0
  constraints (572):
    c: Coincident(g0,g2)
    c: Block(g0)
    c: Block(g1)
    c: Vertical(g3)
    c: Vertical(g4)
    c: Block(g4)
    c: Block(g3)
    c: Tangent(g6,g7) = 1.5708
    c: Tangent(g7,g9) = 1.5708
    c: Equal(g6,g9)
    c: Coincident(g8,g6)
    c: Coincident(g8,g9)
    c: Block(g7)
    c: Block(g8)
    c: Weight(g10) = 1
    c: Equal(g10,g11)
    c: Equal(g10,g12)
    c: InternalAlignment(g10,g13)
    c: InternalAlignment(g11,g13)
    c: InternalAlignment(g12,g13)
    c: InternalAlignment(g14,g13)
    c: InternalAlignment(g15,g13)
    c: Weight(g16) = 1
    c: Equal(g16,g17)
    c: Equal(g16,g18)
    c: InternalAlignment(g16,g19)
    c: InternalAlignment(g17,g19)
    c: InternalAlignment(g18,g19)
    c: InternalAlignment(g20,g19)
    c: InternalAlignment(g21,g19)
    c: Block(g19)
    c: Block(g13)
    c: Weight(g22) = 1
    c: Equal(g22,g23)
    c: Equal(g22,g24)
    c: InternalAlignment(g22,g25)
    c: InternalAlignment(g23,g25)
    c: InternalAlignment(g24,g25)
    c: InternalAlignment(g26,g25)
    c: InternalAlignment(g27,g25)
    c: Weight(g28) = 1
    c: Equal(g28,g29)
    c: Equal(g28,g30)
    c: InternalAlignment(g28,g31)
    c: InternalAlignment(g29,g31)
    c: InternalAlignment(g30,g31)
    c: InternalAlignment(g32,g31)
    c: InternalAlignment(g33,g31)
    c: Block(g31)
    c: Block(g25)
    c: Weight(g34) = 1
    c: Equal(g34,g35)
    c: Equal(g34,g36)
    c: InternalAlignment(g34,g37)
    c: InternalAlignment(g35,g37)
    c: InternalAlignment(g36,g37)
    c: InternalAlignment(g38,g37)
    c: InternalAlignment(g39,g37)
    c: Weight(g40) = 1
    c: Equal(g40,g41)
    c: Equal(g40,g42)
    c: InternalAlignment(g40,g43)
    c: InternalAlignment(g41,g43)
    c: InternalAlignment(g42,g43)
    c: InternalAlignment(g44,g43)
    c: InternalAlignment(g45,g43)
    c: Block(g37)
    c: Block(g43)
    c: Coincident(g46,g4)
    c: Coincident(g46,g3)
    c: Horizontal(g46)
    c: Distance(g46) = 450
    c: Coincident(g47,g4)
    c: Coincident(g47,g3)
    c: Horizontal(g47)
    c: Horizontal(g48)
    c: Coincident(g2,g48)
    c: Block(g48)
    c: Coincident(g1,g48)
    c: Weight(g49) = 1
    c: Equal(g49,g50)
    c: Equal(g49,g51)
    c: InternalAlignment(g49,g52)
    c: InternalAlignment(g50,g52)
    c: InternalAlignment(g51,g52)
    c: InternalAlignment(g53,g52)
    c: InternalAlignment(g54,g52)
    c: Block(g52)
    c: Weight(g55) = 1
    c: Equal(g55,g56)
    c: Equal(g55,g57)
    c: InternalAlignment(g55,g58)
    c: InternalAlignment(g56,g58)
    c: InternalAlignment(g57,g58)
    c: InternalAlignment(g59,g58)
    c: InternalAlignment(g60,g58)
    c: Block(g58)
    c: Weight(g61) = 1
    c: Equal(g61,g62)
    c: Equal(g61,g63)
    c: InternalAlignment(g61,g64)
    c: InternalAlignment(g62,g64)
    c: InternalAlignment(g63,g64)
    c: InternalAlignment(g65,g64)
    c: InternalAlignment(g66,g64)
    c: Block(g64)
    c: Weight(g67) = 1
    c: Equal(g67,g68)
    c: Equal(g67,g69)
    c: InternalAlignment(g67,g70)
    c: InternalAlignment(g68,g70)
    c: InternalAlignment(g69,g70)
    c: InternalAlignment(g71,g70)
    c: InternalAlignment(g72,g70)
    c: Block(g70)
    c: Weight(g73) = 1
    c: Equal(g73,g74)
    c: Equal(g73,g75)
    c: InternalAlignment(g73,g76)
    c: InternalAlignment(g74,g76)
    c: InternalAlignment(g75,g76)
    c: InternalAlignment(g77,g76)
    c: InternalAlignment(g78,g76)
    c: Weight(g79) = 1
    c: Equal(g79,g80)
    c: Equal(g79,g81)
    c: InternalAlignment(g79,g82)
    c: InternalAlignment(g80,g82)
    c: InternalAlignment(g81,g82)
    c: InternalAlignment(g83,g82)
    c: InternalAlignment(g84,g82)
    c: Block(g76)
    c: Block(g82)
    c: Coincident(g85,g76)
    c: Coincident(g85,g82)
    c: Vertical(g85)
    c: Coincident(g86,g76)
    c: Coincident(g86,g58)
    c: Coincident(g87,g58)
    c: Coincident(g87,g82)
    c: Weight(g88) = 1
    c: Equal(g88,g89)
    c: Equal(g88,g90)
    c: InternalAlignment(g88,g91)
    c: InternalAlignment(g89,g91)
    c: InternalAlignment(g90,g91)
    c: InternalAlignment(g92,g91)
    c: InternalAlignment(g93,g91)
    c: Weight(g94) = 1
    c: Equal(g94,g95)
    c: Equal(g94,g96)
    c: InternalAlignment(g94,g97)
    c: InternalAlignment(g95,g97)
    c: InternalAlignment(g96,g97)
    c: InternalAlignment(g98,g97)
    c: InternalAlignment(g99,g97)
    c: Block(g91)
    c: Block(g97)
    c: Coincident(g100,g91)
    c: Coincident(g100,g97)
    c: Vertical(g100)
    c: Coincident(g101,g91)
    c: Coincident(g101,g52)
    c: Coincident(g102,g52)
    c: Coincident(g102,g97)
    c: Weight(g103) = 1
    c: Equal(g103,g104)
    c: Equal(g103,g105)
    c: InternalAlignment(g103,g106)
    c: InternalAlignment(g104,g106)
    c: InternalAlignment(g105,g106)
    c: InternalAlignment(g107,g106)
    c: InternalAlignment(g108,g106)
    c: Weight(g109) = 1
    c: Equal(g109,g110)
    c: Equal(g109,g111)
    c: InternalAlignment(g109,g112)
    c: InternalAlignment(g110,g112)
    c: InternalAlignment(g111,g112)
    c: InternalAlignment(g113,g112)
    c: InternalAlignment(g114,g112)
    c: Block(g106)
    c: Block(g112)
    c: Coincident(g115,g106)
    c: Coincident(g115,g112)
    c: Vertical(g115)
    c: Coincident(g116,g112)
    c: Coincident(g116,g70)
    c: Coincident(g117,g70)
    c: Coincident(g117,g106)
    c: Weight(g118) = 1
    c: Equal(g118,g119)
    c: Equal(g118,g120)
    c: InternalAlignment(g118,g121)
    c: InternalAlignment(g119,g121)
    c: InternalAlignment(g120,g121)
    c: InternalAlignment(g122,g121)
    c: InternalAlignment(g123,g121)
    c: Weight(g124) = 1
    c: Equal(g124,g125)
    c: Equal(g124,g126)
    c: InternalAlignment(g124,g127)
    c: InternalAlignment(g125,g127)
    c: InternalAlignment(g126,g127)
    c: InternalAlignment(g128,g127)
    c: InternalAlignment(g129,g127)
    c: Block(g121)
    c: Block(g127)
    c: Coincident(g130,g121)
    c: Coincident(g130,g127)
    c: Vertical(g130)
    c: Coincident(g131,g127)
    c: Coincident(g131,g64)
    c: Coincident(g132,g64)
    c: Coincident(g132,g121)
    c: Weight(g133) = 1
    c: Equal(g133,g134)
    c: Equal(g133,g135)
    c: InternalAlignment(g133,g136)
    c: InternalAlignment(g134,g136)
    c: InternalAlignment(g135,g136)
    c: InternalAlignment(g137,g136)
    c: InternalAlignment(g138,g136)
    c: Weight(g139) = 1
    c: Equal(g139,g140)
    c: Equal(g139,g141)
    c: InternalAlignment(g139,g142)
    c: InternalAlignment(g140,g142)
    c: InternalAlignment(g141,g142)
    c: InternalAlignment(g143,g142)
    c: InternalAlignment(g144,g142)
    c: Weight(g145) = 1
    c: Equal(g145,g146)
    c: Equal(g145,g147)
    c: InternalAlignment(g145,g148)
    c: InternalAlignment(g146,g148)
    c: InternalAlignment(g147,g148)
    c: InternalAlignment(g149,g148)
    c: InternalAlignment(g150,g148)
    c: Weight(g151) = 1
    c: Equal(g151,g152)
    c: Equal(g151,g153)
    c: InternalAlignment(g151,g154)
    c: InternalAlignment(g152,g154)
    c: InternalAlignment(g153,g154)
    c: InternalAlignment(g155,g154)
    c: InternalAlignment(g156,g154)
    c: Block(g154)
    c: Block(g148)
    c: Block(g142)
    c: Block(g136)
    c: Coincident(g157,g31)
    c: Coincident(g157,g154)
    c: Coincident(g158,g154)
    c: Coincident(g158,g148)
    c: Horizontal(g158)
    c: Coincident(g159,g148)
    c: Coincident(g159,g31)
    c: Vertical(g159)
    c: Coincident(g160,g25)
    c: Coincident(g160,g142)
    c: Vertical(g160)
    c: Coincident(g161,g142)
    c: Coincident(g161,g136)
    c: Horizontal(g161)
    c: Coincident(g162,g136)
    c: Coincident(g162,g25)
    c: Weight(g163) = 1
    c: Equal(g163,g164)
    c: Equal(g163,g165)
    c: InternalAlignment(g163,g166)
    c: InternalAlignment(g164,g166)
    c: InternalAlignment(g165,g166)
    c: InternalAlignment(g167,g166)
    c: InternalAlignment(g168,g166)
    c: Weight(g169) = 1
    c: Equal(g169,g170)
    c: Equal(g169,g171)
    c: InternalAlignment(g169,g172)
    c: InternalAlignment(g170,g172)
    c: InternalAlignment(g171,g172)
    c: InternalAlignment(g173,g172)
    c: InternalAlignment(g174,g172)
    c: Weight(g175) = 1
    c: Equal(g175,g176)
    c: Equal(g175,g177)
    c: InternalAlignment(g175,g178)
    c: InternalAlignment(g176,g178)
    c: InternalAlignment(g177,g178)
    c: InternalAlignment(g179,g178)
    c: InternalAlignment(g180,g178)
    c: Weight(g181) = 1
    c: Equal(g181,g182)
    c: Equal(g181,g183)
    c: InternalAlignment(g181,g184)
    c: InternalAlignment(g182,g184)
    c: InternalAlignment(g183,g184)
    c: InternalAlignment(g185,g184)
    c: InternalAlignment(g186,g184)
    c: Block(g184)
    c: Block(g178)
    c: Block(g172)
    c: Block(g166)
    c: Coincident(g187,g184)
    c: Coincident(g187,g178)
    c: Horizontal(g187)
    c: Coincident(g188,g178)
    c: Coincident(g188,g13)
    c: Vertical(g188)
    c: Coincident(g189,g19)
    c: Coincident(g189,g172)
    c: Vertical(g189)
    c: Coincident(g190,g172)
    c: Coincident(g190,g166)
    c: Horizontal(g190)
    c: Coincident(g191,g166)
    c: Coincident(g191,g19)
    c: Coincident(g192,g13)
    c: Weight(g193) = 1
    c: Equal(g193,g194)
    c: Equal(g193,g195)
    c: InternalAlignment(g193,g196)
    c: InternalAlignment(g194,g196)
    c: InternalAlignment(g195,g196)
    c: InternalAlignment(g197,g196)
    c: InternalAlignment(g198,g196)
    c: Weight(g199) = 1
    c: Equal(g199,g200)
    c: Equal(g199,g201)
    c: InternalAlignment(g199,g202)
    c: InternalAlignment(g200,g202)
    c: InternalAlignment(g201,g202)
    c: InternalAlignment(g203,g202)
    c: InternalAlignment(g204,g202)
    c: Block(g202)
    c: Block(g196)
    c: Coincident(g205,g202)
    c: Coincident(g205,g37)
    c: Coincident(g206,g37)
    c: Coincident(g206,g196)
    c: Coincident(g207,g196)
    c: Coincident(g207,g202)
    c: Vertical(g207)
    c: Weight(g208) = 1
    c: Equal(g208,g209)
    c: Equal(g208,g210)
    c: InternalAlignment(g208,g211)
    c: InternalAlignment(g209,g211)
    c: InternalAlignment(g210,g211)
    c: InternalAlignment(g212,g211)
    c: InternalAlignment(g213,g211)
    c: Weight(g214) = 1
    c: Equal(g214,g215)
    c: Equal(g214,g216)
    c: InternalAlignment(g214,g217)
    c: InternalAlignment(g215,g217)
    c: InternalAlignment(g216,g217)
    c: InternalAlignment(g218,g217)
    c: InternalAlignment(g219,g217)
    c: Block(g217)
    c: Block(g211)
    c: Coincident(g220,g211)
    c: Coincident(g220,g43)
    c: Coincident(g221,g43)
    c: Coincident(g221,g217)
    c: Coincident(g222,g217)
    c: Coincident(g222,g211)
    c: Vertical(g222)
    c: Horizontal(g223)
    c: Block(g223)
    c: Vertical(g224)
    c: Block(g224)
    c: Block(g225)
    c: Weight(g226) = 1
    c: Equal(g226,g227)
    c: Equal(g226,g228)
    c: InternalAlignment(g226,g229)
    c: InternalAlignment(g227,g229)
    c: InternalAlignment(g228,g229)
    c: InternalAlignment(g230,g229)
    c: InternalAlignment(g231,g229)
    c: Weight(g232) = 1
    c: Equal(g232,g233)
    c: Equal(g232,g234)
    c: InternalAlignment(g232,g235)
    c: InternalAlignment(g233,g235)
    c: InternalAlignment(g234,g235)
    c: InternalAlignment(g236,g235)
    c: InternalAlignment(g237,g235)
    c: Weight(g238) = 1
    c: Equal(g238,g239)
    c: Equal(g238,g240)
    c: InternalAlignment(g238,g241)
    c: InternalAlignment(g239,g241)
    c: InternalAlignment(g240,g241)
    c: InternalAlignment(g242,g241)
    c: InternalAlignment(g243,g241)
    c: Weight(g244) = 1
    c: Equal(g244,g245)
    c: Equal(g244,g246)
    c: InternalAlignment(g244,g247)
    c: InternalAlignment(g245,g247)
    c: InternalAlignment(g246,g247)
    c: InternalAlignment(g248,g247)
    c: InternalAlignment(g249,g247)
    c: Block(g229)
    c: Block(g235)
    c: Block(g241)
    c: Block(g247)
    c: Coincident(g250,g235)
    c: Coincident(g250,g229)
    c: Horizontal(g250)
    c: Block(g192)
    c: Weight(g251) = 1
    c: Equal(g251,g252)
    c: Equal(g251,g253)
    c: InternalAlignment(g251,g254)
    c: InternalAlignment(g252,g254)
    c: InternalAlignment(g253,g254)
    c: InternalAlignment(g255,g254)
    c: InternalAlignment(g256,g254)
    c: Weight(g257) = 1
    c: Equal(g257,g258)
    c: Equal(g257,g259)
    c: InternalAlignment(g257,g260)
    c: InternalAlignment(g258,g260)
    c: InternalAlignment(g259,g260)
    c: InternalAlignment(g261,g260)
    c: InternalAlignment(g262,g260)
    c: Block(g254)
    c: Block(g260)
    c: Coincident(g263,g254)
    c: Coincident(g263,g260)
    c: Weight(g264) = 1
    c: Equal(g264,g265)
    c: Equal(g264,g266)
    c: InternalAlignment(g264,g267)
    c: InternalAlignment(g265,g267)
    c: InternalAlignment(g266,g267)
    c: InternalAlignment(g268,g267)
    c: InternalAlignment(g269,g267)
    c: Weight(g270) = 1
    c: Equal(g270,g271)
    c: Equal(g270,g272)
    c: InternalAlignment(g270,g273)
    c: InternalAlignment(g271,g273)
    c: InternalAlignment(g272,g273)
    c: InternalAlignment(g274,g273)
    c: InternalAlignment(g275,g273)
    c: Weight(g276) = 1
    c: Equal(g276,g277)
    c: Equal(g276,g278)
    c: InternalAlignment(g276,g279)
    c: InternalAlignment(g277,g279)
    c: InternalAlignment(g278,g279)
    c: InternalAlignment(g280,g279)
    c: InternalAlignment(g281,g279)
    c: Block(g279)
    c: Block(g273)
    c: Block(g267)
    c: Coincident(g282,g273)
    c: Coincident(g282,g267)
    c: Coincident(g283,g267)
    c: Coincident(g283,g279)
    c: Vertical(g283)
    c: Coincident(g284,g279)
    c: Coincident(g284,g273)
    c: Horizontal(g284)
    c: Weight(g285) = 1
    c: Equal(g285,g286)
    c: InternalAlignment(g285,g287)
    c: InternalAlignment(g286,g287)
    c: InternalAlignment(g288,g287)
    c: InternalAlignment(g289,g287)
    c: Weight(g290) = 1
    c: InternalAlignment(g291,g293)
    c: InternalAlignment(g292,g293)
    c: InternalAlignment(g294,g293)
    c: InternalAlignment(g295,g293)
    c: Weight(g296) = 1
    c: Equal(g296,g297)
    c: Equal(g296,g298)
    c: InternalAlignment(g296,g299)
    c: InternalAlignment(g297,g299)
    c: InternalAlignment(g298,g299)
    c: InternalAlignment(g300,g299)
    c: InternalAlignment(g301,g299)
    c: Equal(g302,g303)
    c: Equal(g302,g304)
    c: InternalAlignment(g302,g305)
    c: InternalAlignment(g303,g305)
    c: InternalAlignment(g304,g305)
    c: InternalAlignment(g306,g305)
    c: InternalAlignment(g307,g305)
    c: Block(g293)
    c: Block(g299)
    c: Block(g305)
    c: Block(g287)
    c: Coincident(g308,g287)
    c: Coincident(g308,g293)
    c: Horizontal(g308)
    c: Coincident(g309,g293)
    c: Coincident(g309,g299)
    c: Vertical(g309)
    c: Coincident(g310,g299)
    c: Coincident(g310,g305)
    c: Horizontal(g310)
    c: Coincident(g311,g305)
    c: Coincident(g311,g287)
    c: Weight(g312) = 1
    c: Equal(g312,g313)
    c: Equal(g312,g314)
    c: InternalAlignment(g312,g315)
    c: InternalAlignment(g313,g315)
    c: InternalAlignment(g314,g315)
    c: InternalAlignment(g316,g315)
    c: InternalAlignment(g317,g315)
    c: Weight(g318) = 1
    c: Equal(g318,g319)
    c: Equal(g318,g320)
    c: InternalAlignment(g318,g321)
    c: InternalAlignment(g319,g321)
    c: InternalAlignment(g320,g321)
    c: InternalAlignment(g322,g321)
    c: InternalAlignment(g323,g321)
    c: Weight(g324) = 1
    c: Equal(g324,g325)
    c: Equal(g324,g326)
    c: InternalAlignment(g324,g327)
    c: InternalAlignment(g325,g327)
    c: InternalAlignment(g326,g327)
    c: InternalAlignment(g328,g327)
    c: InternalAlignment(g329,g327)
    c: Block(g327)
    c: Block(g321)
    c: Block(g315)
    c: Coincident(g330,g327)
    c: Coincident(g330,g321)
    c: Horizontal(g330)
    c: Coincident(g331,g321)
    c: Coincident(g331,g315)
    c: Vertical(g331)
    c: Coincident(g332,g315)
    c: Coincident(g332,g327)
    c: InternalAlignment(g333,g334)
    c: InternalAlignment(g335,g334)
    c: InternalAlignment(g336,g334)
    c: Block(g334)
    c: Equal(g337,g338)
    c: Equal(g337,g339)
    c: InternalAlignment(g337,g340)
    c: InternalAlignment(g338,g340)
    c: InternalAlignment(g339,g340)
    c: InternalAlignment(g341,g340)
    c: InternalAlignment(g342,g340)
    c: Block(g340)
    c: Coincident(g343,g334)
    c: Horizontal(g343)
    c: Block(g343)
    c: Coincident(g344,g334)
    c: Coincident(g344,g260)
    c: Vertical(g344)
    c: Coincident(g345,g340)
    c: Coincident(g345,g254)
    c: Vertical(g345)
    c: Coincident(g347,g5)
    c: Coincident(g348,g5)
    c: Block(g346)
    c: Block(g5)
    c: Block(g348)
    c: Block(g347)
    c: Distance(g344) = 119.89
FEATURE [Sketcher::SketchObject] Sketch001
  FullyConstrained = true
  MapMode = 4
  Placement = pos=(0,0,0) rot=(0.57735,0.57735,0.57735;2.0944rad)
  Support = -> [Sketch]
  sketch-geometry (46):
    g0: BSplineCurve PolesCount=3 KnotsCount=2 Degree=2 IsPeriodic=0
    g1: ArcOfCircle CenterX=73.1223 CenterY=-32.291 CenterZ=0 NormalX=0 NormalY=0 NormalZ=1 AngleXU=0 Radius=13 StartAngle=5.92268 EndAngle=9.06428
    g2: ArcOfCircle CenterX=66.7816 CenterY=-49.1439 CenterZ=0 NormalX=0 NormalY=0 NormalZ=1 AngleXU=0 Radius=13 StartAngle=2.78068 EndAngle=5.92131
    g3: ArcOfCircle CenterX=55.9263 CenterY=-78.1807 CenterZ=0 NormalX=0 NormalY=0 NormalZ=1 AngleXU=0 Radius=13 StartAngle=5.92268 EndAngle=9.06428
    g4: ArcOfCircle CenterX=49.5884 CenterY=-95.0342 CenterZ=0 NormalX=0 NormalY=0 NormalZ=1 AngleXU=0 Radius=13 StartAngle=2.78068 EndAngle=5.92131
    g5: ArcOfCircle CenterX=38.7206 CenterY=-124.067 CenterZ=0 NormalX=0 NormalY=0 NormalZ=1 AngleXU=0 Radius=13 StartAngle=5.92268 EndAngle=9.06428
    g6: ArcOfCircle CenterX=32.3875 CenterY=-140.92 CenterZ=0 NormalX=0 NormalY=0 NormalZ=1 AngleXU=0 Radius=13 StartAngle=2.78068 EndAngle=5.92131
    g7: ArcOfCircle CenterX=21.4715 CenterY=-169.934 CenterZ=0 NormalX=0 NormalY=0 NormalZ=1 AngleXU=0 Radius=13 StartAngle=5.92268 EndAngle=9.06428
    g8: ArcOfCircle CenterX=15.1336 CenterY=-186.787 CenterZ=0 NormalX=0 NormalY=0 NormalZ=1 AngleXU=0 Radius=13 StartAngle=2.78068 EndAngle=5.92131
    g9-g12: Circle x4 (B-spline internal-alignment scaffolding for g13; pole/knot coordinates omitted)
    g13: BSplineCurve PolesCount=4 KnotsCount=2 Degree=3 IsPeriodic=0
    g14: GeomPoint X=28.8094 Y=-19.0875 Z=0
    g15: GeomPoint X=47.0443 Y=-50.4712 Z=0
    g16: Circle CenterX=53.5586 CenterY=-23.2695 CenterZ=0 NormalX=0 NormalY=0 NormalZ=1 AngleXU=0 Radius=3.24518
    g17: Circle CenterX=-195.441 CenterY=-127.082 CenterZ=0 NormalX=0 NormalY=0 NormalZ=1 AngleXU=0 Radius=1
    g18: Circle CenterX=-8.24091 CenterY=-197.481 CenterZ=0 NormalX=0 NormalY=0 NormalZ=1 AngleXU=0 Radius=1
    g19: Circle CenterX=12.8789 CenterY=-141.321 CenterZ=0 NormalX=0 NormalY=0 NormalZ=1 AngleXU=0 Radius=1
    g20: BSplineCurve PolesCount=3 KnotsCount=2 Degree=2 IsPeriodic=0
    g21: GeomPoint X=-195.441 Y=-127.082 Z=0
    g22: GeomPoint X=12.8789 Y=-141.321 Z=0
    g23: Circle CenterX=-12.8016 CenterY=-179.036 CenterZ=0 NormalX=0 NormalY=0 NormalZ=1 AngleXU=0 Radius=10.5072
    g24: Circle CenterX=0.933922 CenterY=-166.43 CenterZ=0 NormalX=0 NormalY=0 NormalZ=1 AngleXU=0 Radius=3.26661
    g25: Circle CenterX=-33.5518 CenterY=-176.44 CenterZ=0 NormalX=0 NormalY=0 NormalZ=1 AngleXU=0 Radius=5.64388
    g26: Circle CenterX=-47.2366 CenterY=-173.859 CenterZ=0 NormalX=0 NormalY=0 NormalZ=1 AngleXU=0 Radius=3.01653
    g27: Circle CenterX=-56.2595 CenterY=-171.456 CenterZ=0 NormalX=0 NormalY=0 NormalZ=1 AngleXU=0 Radius=2.12826
    g28: ArcOfCircle CenterX=51.2151 CenterY=-198.473 CenterZ=0 NormalX=0 NormalY=0 NormalZ=1 AngleXU=0 Radius=20 StartAngle=2.78189 EndAngle=4.35269
    g29: LineSegment StartX=32.4951 StartY=-191.433 StartZ=0 EndX=94.6578 EndY=-26.1352 EndZ=0
    g30: LineSegment StartX=43.1192 StartY=-220.001 StartZ=0 EndX=-196.497 EndY=-129.89 EndZ=0
    g31: LineSegment StartX=43.1192 StartY=-220.001 StartZ=0 EndX=44.1752 EndY=-217.193 EndZ=0
    g32: LineSegment StartX=117.223 StartY=-19.0875 StartZ=0 EndX=117.223 EndY=-16.0875 EndZ=0
    g33: LineSegment StartX=117.223 StartY=-16.0875 StartZ=0 EndX=17.2232 EndY=-16.0875 EndZ=0
    g34: LineSegment StartX=17.2232 StartY=-16.0875 StartZ=0 EndX=17.2232 EndY=-19.0875 EndZ=0
    g35: LineSegment StartX=28.8094 StartY=-19.0875 StartZ=0 EndX=17.2232 EndY=-19.0875 EndZ=0
    g36: LineSegment StartX=47.0443 StartY=-50.4712 StartZ=0 EndX=12.8789 EndY=-141.321 EndZ=0
    g37: LineSegment StartX=-195.441 StartY=-127.082 StartZ=0 EndX=-196.497 EndY=-129.89 EndZ=0
    g38: LineSegment StartX=85.2866 StartY=-36.8766 StartZ=0 EndX=78.9396 EndY=-53.7463 EndZ=0
    g39: LineSegment StartX=60.9579 StartY=-27.7053 StartZ=0 EndX=54.6191 EndY=-44.5532 EndZ=0
    g40: LineSegment StartX=68.0907 StartY=-82.7664 StartZ=0 EndX=61.7465 EndY=-99.6365 EndZ=0
    g41: LineSegment StartX=43.7619 StartY=-73.595 StartZ=0 EndX=37.426 EndY=-90.4435 EndZ=0
    g42: LineSegment StartX=50.885 StartY=-128.652 StartZ=0 EndX=44.5456 EndY=-145.522 EndZ=0
    g43: LineSegment StartX=26.5562 StartY=-119.481 StartZ=0 EndX=20.2251 EndY=-136.329 EndZ=0
    g44: LineSegment StartX=9.3071 StartY=-165.349 StartZ=0 EndX=2.97115 EndY=-182.197 EndZ=0
    g45: LineSegment StartX=33.6358 StartY=-174.52 StartZ=0 EndX=27.2917 EndY=-191.39 EndZ=0
  constraints (71):
    c: Block(g0)
    c: Block(g1)
    c: Block(g2)
    c: Block(g4)
    c: Block(g3)
    c: Block(g6)
    c: Block(g5)
    c: Block(g8)
    c: Block(g7)
    c: Weight(g9) = 1
    c: Equal(g9,g10)
    c: Equal(g9,g11)
    c: Equal(g9,g12)
    c: InternalAlignment(g9-g12 -> g13) x4
    c: InternalAlignment(g14,g13)
    c: InternalAlignment(g15,g13)
    c: Block(g16)
    c: Weight(g17) = 1
    c: Equal(g17,g18)
    c: Equal(g17,g19)
    c: InternalAlignment(g17,g20)
    c: InternalAlignment(g18,g20)
    c: InternalAlignment(g19,g20)
    c: InternalAlignment(g21,g20)
    c: InternalAlignment(g22,g20)
    c: Block(g20)
    c: Block(g23)
    c: Block(g24)
    c: Block(g25)
    c: Block(g26)
    c: Block(g27)
    c: Block(g28)
    c: Coincident(g29,g28)
    c: Coincident(g29,g0)
    c: Block(g13)
    c: Coincident(g31,g30)
    c: Coincident(g31,g28)
    c: Block(g31)
    c: Coincident(g32,g0)
    c: Vertical(g32)
    c: Coincident(g33,g32)
    c: Horizontal(g33)
    c: Coincident(g34,g33)
    c: Vertical(g34)
    c: Block(g33)
    c: Coincident(g35,g13)
    c: Coincident(g35,g34)
    c: Horizontal(g35)
    c: Coincident(g36,g13)
    c: Coincident(g36,g20)
    c: Coincident(g37,g20)
    c: Coincident(g37,g30)
    c: Block(g30)
    c: Coincident(g38,g1)
    c: Coincident(g38,g2)
    c: Coincident(g39,g1)
    c: Coincident(g39,g2)
    c: Coincident(g40,g3)
    c: Coincident(g40,g4)
    c: Coincident(g41,g3)
    c: Coincident(g41,g4)
    c: Coincident(g42,g5)
    c: Coincident(g42,g6)
    c: Coincident(g43,g5)
    c: Coincident(g43,g6)
    c: Coincident(g44,g7)
    c: Coincident(g44,g8)
    c: Coincident(g45,g7)
    c: Coincident(g45,g8)
    c: Distance(g30) = 256
    c: Distance(g33) = 100
FEATURE [Part::Extrusion] Extrude002
  Base = -> Sketch001
  Dir = (1,0,0)
  DirMode = 2
  FaceMakerClass = Part::FaceMakerBullseye
  LengthFwd = 8
  LengthRev = 0
  Solid = true
  Symmetric = false
FEATURE [Sketcher::SketchObject] Sketch002
  FullyConstrained = true
  sketch-geometry (20):
    g0: LineSegment StartX=-2.77179 StartY=-200.304 StartZ=0 EndX=5.22821 EndY=-200.304 EndZ=0
    g1: LineSegment StartX=5.22821 StartY=-200.304 StartZ=0 EndX=5.22821 EndY=-197.304 EndZ=0
    g2: LineSegment StartX=-2.77179 StartY=-200.304 StartZ=0 EndX=-2.77179 EndY=-197.304 EndZ=0
    g3: LineSegment StartX=5.22821 StartY=-197.304 StartZ=0 EndX=8.22821 EndY=-197.304 EndZ=0
    g4: LineSegment StartX=-2.77179 StartY=-197.304 StartZ=0 EndX=-5.77179 EndY=-197.304 EndZ=0
    g5: LineSegment StartX=19.2282 StartY=-203.304 StartZ=0 EndX=19.2282 EndY=-206.304 EndZ=0
    g6: LineSegment StartX=-16.7718 StartY=-203.304 StartZ=0 EndX=-16.7718 EndY=-206.304 EndZ=0
    g7: LineSegment StartX=-16.7718 StartY=-206.304 StartZ=0 EndX=19.2282 EndY=-206.304 EndZ=0
    g8: Circle CenterX=-16.7718 CenterY=-203.304 CenterZ=0 NormalX=0 NormalY=0 NormalZ=1 AngleXU=0 Radius=1
    g9: Circle CenterX=-5.77179 CenterY=-203.304 CenterZ=0 NormalX=0 NormalY=0 NormalZ=1 AngleXU=0 Radius=1
    g10: Circle CenterX=-5.77179 CenterY=-197.304 CenterZ=0 NormalX=0 NormalY=0 NormalZ=1 AngleXU=0 Radius=1
    g11: BSplineCurve PolesCount=3 KnotsCount=2 Degree=2 IsPeriodic=0
    g12: GeomPoint X=-16.7718 Y=-203.304 Z=0
    g13: GeomPoint X=-5.77179 Y=-197.304 Z=0
    g14: Circle CenterX=19.2282 CenterY=-203.304 CenterZ=0 NormalX=0 NormalY=0 NormalZ=1 AngleXU=0 Radius=1
    g15: Circle CenterX=8.22821 CenterY=-203.304 CenterZ=0 NormalX=0 NormalY=0 NormalZ=1 AngleXU=0 Radius=1
    g16: Circle CenterX=8.22821 CenterY=-197.304 CenterZ=0 NormalX=0 NormalY=0 NormalZ=1 AngleXU=0 Radius=1
    g17: BSplineCurve PolesCount=3 KnotsCount=2 Degree=2 IsPeriodic=0
    g18: GeomPoint X=19.2282 Y=-203.304 Z=0
    g19: GeomPoint X=8.22821 Y=-197.304 Z=0
  constraints (41):
    c: Horizontal(g0)
    c: Distance(g0) = 8
    c: Coincident(g1,g0)
    c: Vertical(g1)
    c: Distance(g1) = 3
    c: Coincident(g2,g0)
    c: Vertical(g2)
    c: Distance(g2) = 3
    c: Coincident(g3,g1)
    c: Horizontal(g3)
    c: Distance(g3) = 3
    c: Coincident(g4,g2)
    c: Horizontal(g4)
    c: Distance(g4) = 3
    c: Vertical(g5)
    c: Vertical(g6)
    c: Coincident(g7,g6)
    c: Coincident(g7,g5)
    c: Weight(g8) = 1
    c: Equal(g8,g9)
    c: Equal(g8,g10)
    c: Coincident(g11,g4)
    c: InternalAlignment(g8,g11)
    c: InternalAlignment(g9,g11)
    c: InternalAlignment(g10,g11)
    c: InternalAlignment(g12,g11)
    c: InternalAlignment(g13,g11)
    c: Coincident(g17,g5)
    c: Weight(g14) = 1
    c: Equal(g14,g15)
    c: Equal(g14,g16)
    c: Coincident(g17,g3)
    c: InternalAlignment(g14,g17)
    c: InternalAlignment(g15,g17)
    c: InternalAlignment(g16,g17)
    c: InternalAlignment(g18,g17)
    c: InternalAlignment(g19,g17)
    c: Block(g7)
    c: Block(g17)
    c: Block(g11)
    c: Block(g6)
FEATURE [Part::Extrusion] Extrude003
  Base = -> Sketch002
  Dir = (0,0,1)
  DirMode = 2
  FaceMakerClass = Part::FaceMakerBullseye
  LengthFwd = 260
  LengthRev = 0
  Solid = true
  Symmetric = false
FEATURE [Part::Extrusion] Extrude
  Base = -> Sketch
  Dir = (0,0,1)
  DirMode = 2
  FaceMakerClass = Part::FaceMakerBullseye
  LengthFwd = 14
  LengthRev = 0
  Solid = true
  Symmetric = false
FEATURE [Sketcher::SketchObject] Sketch003
  FullyConstrained = false
  sketch-geometry (369):
    g0: LineSegment StartX=-42.9272 StartY=136.221 StartZ=0 EndX=-42.9272 EndY=-103.779 EndZ=0
    g1: LineSegment StartX=407.073 StartY=136.221 StartZ=0 EndX=407.073 EndY=-103.779 EndZ=0
    g2: ArcOfCircle CenterX=-26.9272 CenterY=-83.7794 CenterZ=0 NormalX=0 NormalY=0 NormalZ=1 AngleXU=0 Radius=8 StartAngle=3.14159 EndAngle=6.28319
    g3: ArcOfCircle CenterX=391.073 CenterY=-83.7794 CenterZ=0 NormalX=0 NormalY=0 NormalZ=1 AngleXU=0 Radius=8 StartAngle=3.14159 EndAngle=6.28319
    g4: Circle CenterX=175.022 CenterY=27.0628 CenterZ=0 NormalX=0 NormalY=0 NormalZ=1 AngleXU=0 Radius=1
    g5: Circle CenterX=179.022 CenterY=24.8665 CenterZ=0 NormalX=0 NormalY=0 NormalZ=1 AngleXU=0 Radius=1
    g6: Circle CenterX=179.022 CenterY=27.0628 CenterZ=0 NormalX=0 NormalY=0 NormalZ=1 AngleXU=0 Radius=1
    g7: BSplineCurve PolesCount=3 KnotsCount=2 Degree=2 IsPeriodic=0
    g8: GeomPoint X=175.022 Y=27.0628 Z=0
    g9: GeomPoint X=179.022 Y=27.0628 Z=0
    g10: Circle CenterX=189.124 CenterY=27.0628 CenterZ=0 NormalX=0 NormalY=0 NormalZ=1 AngleXU=0 Radius=1
    g11: Circle CenterX=185.124 CenterY=24.8665 CenterZ=0 NormalX=0 NormalY=0 NormalZ=1 AngleXU=0 Radius=1
    g12: Circle CenterX=185.124 CenterY=27.0628 CenterZ=0 NormalX=0 NormalY=0 NormalZ=1 AngleXU=0 Radius=1
    g13: BSplineCurve PolesCount=3 KnotsCount=2 Degree=2 IsPeriodic=0
    g14: GeomPoint X=189.124 Y=27.0628 Z=0
    g15: GeomPoint X=185.124 Y=27.0628 Z=0
    g16: Circle CenterX=175.022 CenterY=5.37834 CenterZ=0 NormalX=0 NormalY=0 NormalZ=1 AngleXU=0 Radius=1
    g17: Circle CenterX=179.022 CenterY=7.57463 CenterZ=0 NormalX=0 NormalY=0 NormalZ=1 AngleXU=0 Radius=1
    g18: Circle CenterX=179.022 CenterY=5.34704 CenterZ=0 NormalX=0 NormalY=0 NormalZ=1 AngleXU=0 Radius=1
    g19: BSplineCurve PolesCount=3 KnotsCount=2 Degree=2 IsPeriodic=0
    g20: GeomPoint X=175.022 Y=5.37834 Z=0
    g21: GeomPoint X=179.022 Y=5.34704 Z=0
    g22: Circle CenterX=189.124 CenterY=5.37834 CenterZ=0 NormalX=0 NormalY=0 NormalZ=1 AngleXU=0 Radius=1
    g23: Circle CenterX=185.124 CenterY=7.57463 CenterZ=0 NormalX=0 NormalY=0 NormalZ=1 AngleXU=0 Radius=1
    g24: Circle CenterX=185.124 CenterY=5.34704 CenterZ=0 NormalX=0 NormalY=0 NormalZ=1 AngleXU=0 Radius=1
    g25: BSplineCurve PolesCount=3 KnotsCount=2 Degree=2 IsPeriodic=0
    g26: GeomPoint X=189.124 Y=5.37834 Z=0
    g27: GeomPoint X=185.124 Y=5.34704 Z=0
    g28: Circle CenterX=165.871 CenterY=18.1458 CenterZ=0 NormalX=0 NormalY=0 NormalZ=1 AngleXU=0 Radius=1
    g29: Circle CenterX=169.377 CenterY=16.2206 CenterZ=0 NormalX=0 NormalY=0 NormalZ=1 AngleXU=0 Radius=1
    g30: Circle CenterX=165.871 CenterY=14.2954 CenterZ=0 NormalX=0 NormalY=0 NormalZ=1 AngleXU=0 Radius=1
    g31: BSplineCurve PolesCount=3 KnotsCount=2 Degree=2 IsPeriodic=0
    g32: GeomPoint X=165.871 Y=18.1458 Z=0
    g33: GeomPoint X=165.871 Y=14.2954 Z=0
    g34: Circle CenterX=198.275 CenterY=18.1458 CenterZ=0 NormalX=0 NormalY=0 NormalZ=1 AngleXU=0 Radius=1
    g35: Circle CenterX=194.768 CenterY=16.2206 CenterZ=0 NormalX=0 NormalY=0 NormalZ=1 AngleXU=0 Radius=1
    g36: Circle CenterX=198.275 CenterY=14.2954 CenterZ=0 NormalX=0 NormalY=0 NormalZ=1 AngleXU=0 Radius=1
    g37: BSplineCurve PolesCount=3 KnotsCount=2 Degree=2 IsPeriodic=0
    g38: GeomPoint X=198.275 Y=18.1458 Z=0
    g39: GeomPoint X=198.275 Y=14.2954 Z=0
    g40: LineSegment StartX=407.073 StartY=-103.779 StartZ=0 EndX=-42.9272 EndY=-103.779 EndZ=0
    g41: LineSegment StartX=407.073 StartY=136.221 StartZ=0 EndX=-42.9272 EndY=136.221 EndZ=0
    g42: Circle CenterX=125.607 CenterY=54.1951 CenterZ=0 NormalX=0 NormalY=0 NormalZ=1 AngleXU=0 Radius=1
    g43: Circle CenterX=139.632 CenterY=46.4944 CenterZ=0 NormalX=0 NormalY=0 NormalZ=1 AngleXU=0 Radius=1
    g44: Circle CenterX=127.326 CenterY=56.7187 CenterZ=0 NormalX=0 NormalY=0 NormalZ=1 AngleXU=0 Radius=1
    g45: BSplineCurve PolesCount=3 KnotsCount=2 Degree=2 IsPeriodic=0
    g46: GeomPoint X=125.607 Y=54.1951 Z=0
    g47: GeomPoint X=127.326 Y=56.7187 Z=0
    g48: Circle CenterX=236.821 CenterY=56.7187 CenterZ=0 NormalX=0 NormalY=0 NormalZ=1 AngleXU=0 Radius=1
    g49: Circle CenterX=224.513 CenterY=46.4944 CenterZ=0 NormalX=0 NormalY=0 NormalZ=1 AngleXU=0 Radius=1
    g50: Circle CenterX=238.538 CenterY=54.1951 CenterZ=0 NormalX=0 NormalY=0 NormalZ=1 AngleXU=0 Radius=1
    g51: BSplineCurve PolesCount=3 KnotsCount=2 Degree=2 IsPeriodic=0
    g52: GeomPoint X=236.821 Y=56.7187 Z=0
    g53: GeomPoint X=238.538 Y=54.1951 Z=0
    g54: Circle CenterX=238.538 CenterY=-21.7539 CenterZ=0 NormalX=0 NormalY=0 NormalZ=1 AngleXU=0 Radius=1
    g55: Circle CenterX=224.513 CenterY=-14.0532 CenterZ=0 NormalX=0 NormalY=0 NormalZ=1 AngleXU=0 Radius=1
    g56: Circle CenterX=236.821 CenterY=-24.2775 CenterZ=0 NormalX=0 NormalY=0 NormalZ=1 AngleXU=0 Radius=1
    g57: BSplineCurve PolesCount=3 KnotsCount=2 Degree=2 IsPeriodic=0
    g58: GeomPoint X=238.538 Y=-21.7539 Z=0
    g59: GeomPoint X=236.821 Y=-24.2775 Z=0
    g60: Circle CenterX=125.607 CenterY=-21.7539 CenterZ=0 NormalX=0 NormalY=0 NormalZ=1 AngleXU=0 Radius=1
    g61: Circle CenterX=139.632 CenterY=-14.0532 CenterZ=0 NormalX=0 NormalY=0 NormalZ=1 AngleXU=0 Radius=1
    g62: Circle CenterX=127.325 CenterY=-24.2775 CenterZ=0 NormalX=0 NormalY=0 NormalZ=1 AngleXU=0 Radius=1
    g63: BSplineCurve PolesCount=3 KnotsCount=2 Degree=2 IsPeriodic=0
    g64: GeomPoint X=125.607 Y=-21.7539 Z=0
    g65: GeomPoint X=127.325 Y=-24.2775 Z=0
    g66: Circle CenterX=302.996 CenterY=111.695 CenterZ=0 NormalX=0 NormalY=0 NormalZ=1 AngleXU=0 Radius=1
    g67: Circle CenterX=306.073 CenterY=114.251 CenterZ=0 NormalX=0 NormalY=0 NormalZ=1 AngleXU=0 Radius=1
    g68: Circle CenterX=306.073 CenterY=110.251 CenterZ=0 NormalX=0 NormalY=0 NormalZ=1 AngleXU=0 Radius=1
    g69: BSplineCurve PolesCount=3 KnotsCount=2 Degree=2 IsPeriodic=0
    g70: GeomPoint X=302.996 Y=111.695 Z=0
    g71: GeomPoint X=306.073 Y=110.251 Z=0
    g72: Circle CenterX=306.073 CenterY=95.2763 CenterZ=0 NormalX=0 NormalY=0 NormalZ=1 AngleXU=0 Radius=1
    g73: Circle CenterX=306.073 CenterY=91.2763 CenterZ=0 NormalX=0 NormalY=0 NormalZ=1 AngleXU=0 Radius=1
    g74: Circle CenterX=302.567 CenterY=89.3511 CenterZ=0 NormalX=0 NormalY=0 NormalZ=1 AngleXU=0 Radius=1
    g75: BSplineCurve PolesCount=3 KnotsCount=2 Degree=2 IsPeriodic=0
    g76: GeomPoint X=306.073 Y=95.2763 Z=0
    g77: GeomPoint X=302.567 Y=89.3511 Z=0
    g78: LineSegment StartX=306.073 StartY=110.251 StartZ=0 EndX=306.073 EndY=95.2763 EndZ=0
    g79: LineSegment StartX=302.996 StartY=111.695 StartZ=0 EndX=236.821 EndY=56.7187 EndZ=0
    g80: LineSegment StartX=238.538 StartY=54.1951 StartZ=0 EndX=302.567 EndY=89.3511 EndZ=0
    g81: Circle CenterX=61.1496 CenterY=111.695 CenterZ=0 NormalX=0 NormalY=0 NormalZ=1 AngleXU=0 Radius=1
    g82: Circle CenterX=58.0728 CenterY=114.251 CenterZ=0 NormalX=0 NormalY=0 NormalZ=1 AngleXU=0 Radius=1
    g83: Circle CenterX=58.0728 CenterY=110.251 CenterZ=0 NormalX=0 NormalY=0 NormalZ=1 AngleXU=0 Radius=1
    g84: BSplineCurve PolesCount=3 KnotsCount=2 Degree=2 IsPeriodic=0
    g85: GeomPoint X=61.1496 Y=111.695 Z=0
    g86: GeomPoint X=58.0728 Y=110.251 Z=0
    g87: Circle CenterX=61.5791 CenterY=89.3511 CenterZ=0 NormalX=0 NormalY=0 NormalZ=1 AngleXU=0 Radius=1
    g88: Circle CenterX=58.0728 CenterY=91.2763 CenterZ=0 NormalX=0 NormalY=0 NormalZ=1 AngleXU=0 Radius=1
    g89: Circle CenterX=58.0728 CenterY=95.2763 CenterZ=0 NormalX=0 NormalY=0 NormalZ=1 AngleXU=0 Radius=1
    g90: BSplineCurve PolesCount=3 KnotsCount=2 Degree=2 IsPeriodic=0
    g91: GeomPoint X=61.5791 Y=89.3511 Z=0
    g92: GeomPoint X=58.0728 Y=95.2763 Z=0
    g93: LineSegment StartX=58.0728 StartY=110.251 StartZ=0 EndX=58.0728 EndY=95.2763 EndZ=0
    g94: LineSegment StartX=61.1496 StartY=111.695 StartZ=0 EndX=127.326 EndY=56.7187 EndZ=0
    g95: LineSegment StartX=125.607 StartY=54.1951 StartZ=0 EndX=61.5791 EndY=89.3511 EndZ=0
    g96: Circle CenterX=61.5791 CenterY=-56.9099 CenterZ=0 NormalX=0 NormalY=0 NormalZ=1 AngleXU=0 Radius=1
    g97: Circle CenterX=58.0728 CenterY=-58.8351 CenterZ=0 NormalX=0 NormalY=0 NormalZ=1 AngleXU=0 Radius=1
    g98: Circle CenterX=58.0728 CenterY=-62.8351 CenterZ=0 NormalX=0 NormalY=0 NormalZ=1 AngleXU=0 Radius=1
    g99: BSplineCurve PolesCount=3 KnotsCount=2 Degree=2 IsPeriodic=0
    g100: GeomPoint X=61.5791 Y=-56.9099 Z=0
    g101: GeomPoint X=58.0728 Y=-62.8351 Z=0
    g102: Circle CenterX=58.0728 CenterY=-77.8102 CenterZ=0 NormalX=0 NormalY=0 NormalZ=1 AngleXU=0 Radius=1
    g103: Circle CenterX=58.0728 CenterY=-81.8102 CenterZ=0 NormalX=0 NormalY=0 NormalZ=1 AngleXU=0 Radius=1
    g104: Circle CenterX=61.1496 CenterY=-79.2541 CenterZ=0 NormalX=0 NormalY=0 NormalZ=1 AngleXU=0 Radius=1
    g105: BSplineCurve PolesCount=3 KnotsCount=2 Degree=2 IsPeriodic=0
    g106: GeomPoint X=58.0728 Y=-77.8102 Z=0
    g107: GeomPoint X=61.1496 Y=-79.2541 Z=0
    g108: LineSegment StartX=58.0728 StartY=-62.8351 StartZ=0 EndX=58.0728 EndY=-77.8102 EndZ=0
    g109: LineSegment StartX=61.1496 StartY=-79.2541 StartZ=0 EndX=127.325 EndY=-24.2775 EndZ=0
    g110: LineSegment StartX=125.607 StartY=-21.7539 StartZ=0 EndX=61.5791 EndY=-56.9099 EndZ=0
    g111: Circle CenterX=302.567 CenterY=-56.9099 CenterZ=0 NormalX=0 NormalY=0 NormalZ=1 AngleXU=0 Radius=1
    g112: Circle CenterX=306.073 CenterY=-58.8351 CenterZ=0 NormalX=0 NormalY=0 NormalZ=1 AngleXU=0 Radius=1
    g113: Circle CenterX=306.073 CenterY=-62.8351 CenterZ=0 NormalX=0 NormalY=0 NormalZ=1 AngleXU=0 Radius=1
    g114: BSplineCurve PolesCount=3 KnotsCount=2 Degree=2 IsPeriodic=0
    g115: GeomPoint X=302.567 Y=-56.9099 Z=0
    g116: GeomPoint X=306.073 Y=-62.8351 Z=0
    g117: Circle CenterX=302.996 CenterY=-79.2541 CenterZ=0 NormalX=0 NormalY=0 NormalZ=1 AngleXU=0 Radius=1
    g118: Circle CenterX=306.073 CenterY=-81.8102 CenterZ=0 NormalX=0 NormalY=0 NormalZ=1 AngleXU=0 Radius=1
    g119: Circle CenterX=306.073 CenterY=-77.8102 CenterZ=0 NormalX=0 NormalY=0 NormalZ=1 AngleXU=0 Radius=1
    g120: BSplineCurve PolesCount=3 KnotsCount=2 Degree=2 IsPeriodic=0
    g121: GeomPoint X=302.996 Y=-79.2541 Z=0
    g122: GeomPoint X=306.073 Y=-77.8102 Z=0
    g123: LineSegment StartX=306.073 StartY=-62.8351 StartZ=0 EndX=306.073 EndY=-77.8102 EndZ=0
    g124: LineSegment StartX=302.996 StartY=-79.2541 StartZ=0 EndX=236.821 EndY=-24.2775 EndZ=0
    g125: LineSegment StartX=238.538 StartY=-21.7539 StartZ=0 EndX=302.567 EndY=-56.9099 EndZ=0
    g126: Circle CenterX=61.6457 CenterY=-88.8112 CenterZ=0 NormalX=0 NormalY=0 NormalZ=1 AngleXU=0 Radius=1
    g127: Circle CenterX=58.0728 CenterY=-91.7794 CenterZ=0 NormalX=0 NormalY=0 NormalZ=1 AngleXU=0 Radius=1
    g128: Circle CenterX=63.9135 CenterY=-91.7794 CenterZ=0 NormalX=0 NormalY=0 NormalZ=1 AngleXU=0 Radius=1
    g129: BSplineCurve PolesCount=3 KnotsCount=2 Degree=2 IsPeriodic=0
    g130: GeomPoint X=61.6457 Y=-88.8112 Z=0
    g131: GeomPoint X=63.9135 Y=-91.7794 Z=0
    g132: Circle CenterX=179.022 CenterY=-85.8163 CenterZ=0 NormalX=0 NormalY=0 NormalZ=1 AngleXU=0 Radius=1
    g133: Circle CenterX=179.022 CenterY=-91.7794 CenterZ=0 NormalX=0 NormalY=0 NormalZ=1 AngleXU=0 Radius=1
    g134: Circle CenterX=171.895 CenterY=-91.7794 CenterZ=0 NormalX=0 NormalY=0 NormalZ=1 AngleXU=0 Radius=1
    g135: BSplineCurve PolesCount=3 KnotsCount=2 Degree=2 IsPeriodic=0
    g136: GeomPoint X=179.022 Y=-85.8163 Z=0
    g137: GeomPoint X=171.895 Y=-91.7794 Z=0
    g138: Circle CenterX=185.124 CenterY=-86.2028 CenterZ=0 NormalX=0 NormalY=0 NormalZ=1 AngleXU=0 Radius=1
    g139: Circle CenterX=185.124 CenterY=-91.7794 CenterZ=0 NormalX=0 NormalY=0 NormalZ=1 AngleXU=0 Radius=1
    g140: Circle CenterX=191.747 CenterY=-91.7794 CenterZ=0 NormalX=0 NormalY=0 NormalZ=1 AngleXU=0 Radius=1
    g141: BSplineCurve PolesCount=3 KnotsCount=2 Degree=2 IsPeriodic=0
    g142: GeomPoint X=185.124 Y=-86.2028 Z=0
    g143: GeomPoint X=191.747 Y=-91.7794 Z=0
    g144: Circle CenterX=299.888 CenterY=-86.6413 CenterZ=0 NormalX=0 NormalY=0 NormalZ=1 AngleXU=0 Radius=1
    g145: Circle CenterX=306.073 CenterY=-91.7794 CenterZ=0 NormalX=0 NormalY=0 NormalZ=1 AngleXU=0 Radius=1
    g146: Circle CenterX=298.776 CenterY=-91.7794 CenterZ=0 NormalX=0 NormalY=0 NormalZ=1 AngleXU=0 Radius=1
    g147: BSplineCurve PolesCount=3 KnotsCount=2 Degree=2 IsPeriodic=0
    g148: GeomPoint X=299.888 Y=-86.6413 Z=0
    g149: GeomPoint X=298.776 Y=-91.7794 Z=0
    g150: LineSegment StartX=189.124 StartY=5.37834 StartZ=0 EndX=299.888 EndY=-86.6413 EndZ=0
    g151: LineSegment StartX=298.776 StartY=-91.7794 StartZ=0 EndX=191.747 EndY=-91.7794 EndZ=0
    g152: LineSegment StartX=185.124 StartY=-86.2028 StartZ=0 EndX=185.124 EndY=5.34704 EndZ=0
    g153: LineSegment StartX=179.022 StartY=5.34704 StartZ=0 EndX=179.022 EndY=-85.8163 EndZ=0
    g154: LineSegment StartX=171.895 StartY=-91.7794 StartZ=0 EndX=63.9135 EndY=-91.7794 EndZ=0
    g155: LineSegment StartX=61.6457 StartY=-88.8112 StartZ=0 EndX=175.022 EndY=5.37834 EndZ=0
    g156: Circle CenterX=302.073 CenterY=124.221 CenterZ=0 NormalX=0 NormalY=0 NormalZ=1 AngleXU=0 Radius=1
    g157: Circle CenterX=306.073 CenterY=124.221 CenterZ=0 NormalX=0 NormalY=0 NormalZ=1 AngleXU=0 Radius=1
    g158: Circle CenterX=302.996 CenterY=121.665 CenterZ=0 NormalX=0 NormalY=0 NormalZ=1 AngleXU=0 Radius=1
    g159: BSplineCurve PolesCount=3 KnotsCount=2 Degree=2 IsPeriodic=0
    g160: GeomPoint X=302.073 Y=124.221 Z=0
    g161: GeomPoint X=302.996 Y=121.665 Z=0
    g162: Circle CenterX=189.124 CenterY=124.221 CenterZ=0 NormalX=0 NormalY=0 NormalZ=1 AngleXU=0 Radius=1
    g163: Circle CenterX=185.124 CenterY=124.221 CenterZ=0 NormalX=0 NormalY=0 NormalZ=1 AngleXU=0 Radius=1
    g164: Circle CenterX=185.124 CenterY=120.221 CenterZ=0 NormalX=0 NormalY=0 NormalZ=1 AngleXU=0 Radius=1
    g165: BSplineCurve PolesCount=3 KnotsCount=2 Degree=2 IsPeriodic=0
    g166: GeomPoint X=189.124 Y=124.221 Z=0
    g167: GeomPoint X=185.124 Y=120.221 Z=0
    g168: Circle CenterX=175.022 CenterY=124.221 CenterZ=0 NormalX=0 NormalY=0 NormalZ=1 AngleXU=0 Radius=1
    g169: Circle CenterX=179.022 CenterY=124.221 CenterZ=0 NormalX=0 NormalY=0 NormalZ=1 AngleXU=0 Radius=1
    g170: Circle CenterX=179.022 CenterY=120.221 CenterZ=0 NormalX=0 NormalY=0 NormalZ=1 AngleXU=0 Radius=1
    g171: BSplineCurve PolesCount=3 KnotsCount=2 Degree=2 IsPeriodic=0
    g172: GeomPoint X=175.022 Y=124.221 Z=0
    g173: GeomPoint X=179.022 Y=120.221 Z=0
    g174: Circle CenterX=62.0728 CenterY=124.221 CenterZ=0 NormalX=0 NormalY=0 NormalZ=1 AngleXU=0 Radius=1
    g175: Circle CenterX=58.0728 CenterY=124.221 CenterZ=0 NormalX=0 NormalY=0 NormalZ=1 AngleXU=0 Radius=1
    g176: Circle CenterX=61.1496 CenterY=121.665 CenterZ=0 NormalX=0 NormalY=0 NormalZ=1 AngleXU=0 Radius=1
    g177: BSplineCurve PolesCount=3 KnotsCount=2 Degree=2 IsPeriodic=0
    g178: GeomPoint X=62.0728 Y=124.221 Z=0
    g179: GeomPoint X=61.1496 Y=121.665 Z=0
    g180: LineSegment StartX=62.0728 StartY=124.221 StartZ=0 EndX=175.022 EndY=124.221 EndZ=0
    g181: LineSegment StartX=179.022 StartY=120.221 StartZ=0 EndX=179.022 EndY=27.0628 EndZ=0
    g182: LineSegment StartX=185.124 StartY=27.0628 StartZ=0 EndX=185.124 EndY=120.221 EndZ=0
    g183: LineSegment StartX=189.124 StartY=124.221 StartZ=0 EndX=302.073 EndY=124.221 EndZ=0
    g184: LineSegment StartX=302.996 StartY=121.665 StartZ=0 EndX=189.124 EndY=27.0628 EndZ=0
    g185: LineSegment StartX=175.022 StartY=27.0628 StartZ=0 EndX=61.1496 EndY=121.665 EndZ=0
    g186: Circle CenterX=61.5791 CenterY=75.4095 CenterZ=0 NormalX=0 NormalY=0 NormalZ=1 AngleXU=0 Radius=1
    g187: Circle CenterX=58.0728 CenterY=77.3346 CenterZ=0 NormalX=0 NormalY=0 NormalZ=1 AngleXU=0 Radius=1
    g188: Circle CenterX=58.0728 CenterY=73.3346 CenterZ=0 NormalX=0 NormalY=0 NormalZ=1 AngleXU=0 Radius=1
    g189: BSplineCurve PolesCount=3 KnotsCount=2 Degree=2 IsPeriodic=0
    g190: GeomPoint X=61.5791 Y=75.4095 Z=0
    g191: GeomPoint X=58.0728 Y=73.3346 Z=0
    g192: Circle CenterX=58.0728 CenterY=-40.8935 CenterZ=0 NormalX=0 NormalY=0 NormalZ=1 AngleXU=0 Radius=1
    g193: Circle CenterX=58.0728 CenterY=-44.8935 CenterZ=0 NormalX=0 NormalY=0 NormalZ=1 AngleXU=0 Radius=1
    g194: Circle CenterX=61.5791 CenterY=-42.9683 CenterZ=0 NormalX=0 NormalY=0 NormalZ=1 AngleXU=0 Radius=1
    g195: BSplineCurve PolesCount=3 KnotsCount=2 Degree=2 IsPeriodic=0
    g196: GeomPoint X=58.0728 Y=-40.8935 Z=0
    g197: GeomPoint X=61.5791 Y=-42.9683 Z=0
    g198: LineSegment StartX=61.5791 StartY=-42.9683 StartZ=0 EndX=165.871 EndY=14.2954 EndZ=0
    g199: LineSegment StartX=165.871 StartY=18.1458 StartZ=0 EndX=61.5791 EndY=75.4095 EndZ=0
    g200: LineSegment StartX=58.0728 StartY=73.3346 StartZ=0 EndX=58.0728 EndY=-40.8935 EndZ=0
    g201: Circle CenterX=302.567 CenterY=-42.9683 CenterZ=0 NormalX=0 NormalY=0 NormalZ=1 AngleXU=0 Radius=1
    g202: Circle CenterX=306.073 CenterY=-44.8935 CenterZ=0 NormalX=0 NormalY=0 NormalZ=1 AngleXU=0 Radius=1
    g203: Circle CenterX=306.073 CenterY=-40.8935 CenterZ=0 NormalX=0 NormalY=0 NormalZ=1 AngleXU=0 Radius=1
    g204: BSplineCurve PolesCount=3 KnotsCount=2 Degree=2 IsPeriodic=0
    g205: GeomPoint X=302.567 Y=-42.9683 Z=0
    g206: GeomPoint X=306.073 Y=-40.8935 Z=0
    g207: Circle CenterX=306.073 CenterY=73.3346 CenterZ=0 NormalX=0 NormalY=0 NormalZ=1 AngleXU=0 Radius=1
    g208: Circle CenterX=306.073 CenterY=77.3346 CenterZ=0 NormalX=0 NormalY=0 NormalZ=1 AngleXU=0 Radius=1
    g209: Circle CenterX=302.567 CenterY=75.4095 CenterZ=0 NormalX=0 NormalY=0 NormalZ=1 AngleXU=0 Radius=1
    g210: BSplineCurve PolesCount=3 KnotsCount=2 Degree=2 IsPeriodic=0
    g211: GeomPoint X=306.073 Y=73.3346 Z=0
    g212: GeomPoint X=302.567 Y=75.4095 Z=0
    g213: LineSegment StartX=302.567 StartY=-42.9683 StartZ=0 EndX=198.275 EndY=14.2954 EndZ=0
    g214: LineSegment StartX=198.275 StartY=18.1458 StartZ=0 EndX=302.567 EndY=75.4095 EndZ=0
    g215: LineSegment StartX=306.073 StartY=73.3346 StartZ=0 EndX=306.073 EndY=-40.8935 EndZ=0
    g216: LineSegment StartX=322.073 StartY=105.865 StartZ=0 EndX=328.643 EndY=105.865 EndZ=0
    g217: LineSegment StartX=318.073 StartY=120.221 StartZ=0 EndX=318.073 EndY=109.865 EndZ=0
    g218: LineSegment StartX=336.157 StartY=107.779 StartZ=0 EndX=362.567 EndY=122.294 EndZ=0
    g219: Circle CenterX=362.073 CenterY=124.221 CenterZ=0 NormalX=0 NormalY=0 NormalZ=1 AngleXU=0 Radius=1
    g220: Circle CenterX=366.073 CenterY=124.221 CenterZ=0 NormalX=0 NormalY=0 NormalZ=1 AngleXU=0 Radius=1
    g221: Circle CenterX=362.567 CenterY=122.294 CenterZ=0 NormalX=0 NormalY=0 NormalZ=1 AngleXU=0 Radius=1
    g222: BSplineCurve PolesCount=3 KnotsCount=2 Degree=2 IsPeriodic=0
    g223: GeomPoint X=362.073 Y=124.221 Z=0
    g224: GeomPoint X=362.567 Y=122.294 Z=0
    g225: Circle CenterX=322.073 CenterY=124.221 CenterZ=0 NormalX=0 NormalY=0 NormalZ=1 AngleXU=0 Radius=1
    g226: Circle CenterX=318.073 CenterY=124.221 CenterZ=0 NormalX=0 NormalY=0 NormalZ=1 AngleXU=0 Radius=1
    g227: Circle CenterX=318.073 CenterY=120.221 CenterZ=0 NormalX=0 NormalY=0 NormalZ=1 AngleXU=0 Radius=1
    g228: BSplineCurve PolesCount=3 KnotsCount=2 Degree=2 IsPeriodic=0
    g229: GeomPoint X=322.073 Y=124.221 Z=0
    g230: GeomPoint X=318.073 Y=120.221 Z=0
    g231: Circle CenterX=322.073 CenterY=105.865 CenterZ=0 NormalX=0 NormalY=0 NormalZ=1 AngleXU=0 Radius=1
    g232: Circle CenterX=318.073 CenterY=105.865 CenterZ=0 NormalX=0 NormalY=0 NormalZ=1 AngleXU=0 Radius=1
    g233: Circle CenterX=318.073 CenterY=109.865 CenterZ=0 NormalX=0 NormalY=0 NormalZ=1 AngleXU=0 Radius=1
    g234: BSplineCurve PolesCount=3 KnotsCount=2 Degree=2 IsPeriodic=0
    g235: GeomPoint X=322.073 Y=105.865 Z=0
    g236: GeomPoint X=318.073 Y=109.865 Z=0
    g237: Circle CenterX=336.157 CenterY=107.779 CenterZ=0 NormalX=0 NormalY=0 NormalZ=1 AngleXU=0 Radius=1
    g238: Circle CenterX=332.651 CenterY=105.853 CenterZ=0 NormalX=0 NormalY=0 NormalZ=1 AngleXU=0 Radius=1
    g239: Circle CenterX=328.643 CenterY=105.865 CenterZ=0 NormalX=0 NormalY=0 NormalZ=1 AngleXU=0 Radius=1
    g240: BSplineCurve PolesCount=3 KnotsCount=2 Degree=2 IsPeriodic=0
    g241: GeomPoint X=336.157 Y=107.779 Z=0
    g242: GeomPoint X=328.643 Y=105.865 Z=0
    g243: LineSegment StartX=322.073 StartY=124.221 StartZ=0 EndX=362.073 EndY=124.221 EndZ=0
    g244: Circle CenterX=371.567 CenterY=-80.8644 CenterZ=0 NormalX=0 NormalY=0 NormalZ=1 AngleXU=0 Radius=1
    g245: Circle CenterX=375.073 CenterY=-82.7896 CenterZ=0 NormalX=0 NormalY=0 NormalZ=1 AngleXU=0 Radius=1
    g246: Circle CenterX=375.073 CenterY=-78.7896 CenterZ=0 NormalX=0 NormalY=0 NormalZ=1 AngleXU=0 Radius=1
    g247: BSplineCurve PolesCount=3 KnotsCount=2 Degree=2 IsPeriodic=0
    g248: GeomPoint X=371.567 Y=-80.8644 Z=0
    g249: GeomPoint X=375.073 Y=-78.7896 Z=0
    g250: Circle CenterX=321.579 CenterY=-53.4075 CenterZ=0 NormalX=0 NormalY=0 NormalZ=1 AngleXU=0 Radius=1
    g251: Circle CenterX=318.073 CenterY=-51.4823 CenterZ=0 NormalX=0 NormalY=0 NormalZ=1 AngleXU=0 Radius=1
    g252: Circle CenterX=318.073 CenterY=-47.4805 CenterZ=0 NormalX=0 NormalY=0 NormalZ=1 AngleXU=0 Radius=1
    g253: BSplineCurve PolesCount=3 KnotsCount=2 Degree=2 IsPeriodic=0
    g254: GeomPoint X=321.579 Y=-53.4075 Z=0
    g255: GeomPoint X=318.073 Y=-47.4805 Z=0
    g256: LineSegment StartX=371.567 StartY=-80.8644 StartZ=0 EndX=321.579 EndY=-53.4075 EndZ=0
    g257: Circle CenterX=321.579 CenterY=-67.3492 CenterZ=0 NormalX=0 NormalY=0 NormalZ=1 AngleXU=0 Radius=1
    g258: Circle CenterX=318.073 CenterY=-65.424 CenterZ=0 NormalX=0 NormalY=0 NormalZ=1 AngleXU=0 Radius=1
    g259: Circle CenterX=318.073 CenterY=-69.424 CenterZ=0 NormalX=0 NormalY=0 NormalZ=1 AngleXU=0 Radius=1
    g260: BSplineCurve PolesCount=3 KnotsCount=2 Degree=2 IsPeriodic=0
    g261: GeomPoint X=321.579 Y=-67.3492 Z=0
    g262: GeomPoint X=318.073 Y=-69.424 Z=0
    g263: Circle CenterX=362.567 CenterY=-89.8542 CenterZ=0 NormalX=0 NormalY=0 NormalZ=1 AngleXU=0 Radius=1
    g264: Circle CenterX=366.073 CenterY=-91.7794 CenterZ=0 NormalX=0 NormalY=0 NormalZ=1 AngleXU=0 Radius=1
    g265: Circle CenterX=362.073 CenterY=-91.7794 CenterZ=0 NormalX=0 NormalY=0 NormalZ=1 AngleXU=0 Radius=1
    g266: BSplineCurve PolesCount=3 KnotsCount=2 Degree=2 IsPeriodic=0
    g267: GeomPoint X=362.567 Y=-89.8542 Z=0
    g268: GeomPoint X=362.073 Y=-91.7794 Z=0
    g269: Circle CenterX=322.073 CenterY=-91.7794 CenterZ=0 NormalX=0 NormalY=0 NormalZ=1 AngleXU=0 Radius=1
    g270: Circle CenterX=318.073 CenterY=-91.7794 CenterZ=0 NormalX=0 NormalY=0 NormalZ=1 AngleXU=0 Radius=1
    g271: Circle CenterX=318.073 CenterY=-87.7794 CenterZ=0 NormalX=0 NormalY=0 NormalZ=1 AngleXU=0 Radius=1
    g272: BSplineCurve PolesCount=3 KnotsCount=2 Degree=2 IsPeriodic=0
    g273: GeomPoint X=322.073 Y=-91.7794 Z=0
    g274: GeomPoint X=318.073 Y=-87.7794 Z=0
    g275: LineSegment StartX=362.567 StartY=-89.8542 StartZ=0 EndX=321.579 EndY=-67.3492 EndZ=0
    g276: LineSegment StartX=318.073 StartY=-69.424 StartZ=0 EndX=318.073 EndY=-87.7794 EndZ=0
    g277: LineSegment StartX=322.073 StartY=-91.7794 StartZ=0 EndX=362.073 EndY=-91.7794 EndZ=0
    g278: Circle CenterX=2.07281 CenterY=124.221 CenterZ=0 NormalX=0 NormalY=0 NormalZ=1 AngleXU=0 Radius=1
    g279: Circle CenterX=1.57905 CenterY=122.295 CenterZ=0 NormalX=0 NormalY=0 NormalZ=1 AngleXU=0 Radius=1
    g280: BSplineCurve PolesCount=3 KnotsCount=2 Degree=2 IsPeriodic=0
    g281: GeomPoint X=2.07281 Y=124.221 Z=0
    g282: GeomPoint X=1.57905 Y=122.295 Z=0
    g283: Circle CenterX=42.0728 CenterY=124.221 CenterZ=0 NormalX=0 NormalY=0 NormalZ=1 AngleXU=0 Radius=1
    g284: Circle CenterX=46.0728 CenterY=124.221 CenterZ=0 NormalX=0 NormalY=0 NormalZ=1 AngleXU=0 Radius=1
    g285: Circle CenterX=46.0728 CenterY=120.221 CenterZ=0 NormalX=0 NormalY=0 NormalZ=1 AngleXU=0 Radius=1
    g286: BSplineCurve PolesCount=3 KnotsCount=2 Degree=2 IsPeriodic=0
    g287: GeomPoint X=42.0728 Y=124.221 Z=0
    g288: GeomPoint X=46.0728 Y=120.221 Z=0
    g289: Circle CenterX=46.0728 CenterY=109.865 CenterZ=0 NormalX=0 NormalY=0 NormalZ=1 AngleXU=0 Radius=1
    g290: Circle CenterX=46.0728 CenterY=105.865 CenterZ=0 NormalX=0 NormalY=0 NormalZ=1 AngleXU=0 Radius=1
    g291: Circle CenterX=42.0728 CenterY=105.865 CenterZ=0 NormalX=0 NormalY=0 NormalZ=1 AngleXU=0 Radius=1
    g292: BSplineCurve PolesCount=3 KnotsCount=2 Degree=2 IsPeriodic=0
    g293: GeomPoint X=46.0728 Y=109.865 Z=0
    g294: GeomPoint X=42.0728 Y=105.865 Z=0
    g295: Circle CenterX=35.5028 CenterY=105.865 CenterZ=0 NormalX=0 NormalY=0 NormalZ=1 AngleXU=0 Radius=1
    g296: Circle CenterX=31.5028 CenterY=105.865 CenterZ=0 NormalX=0 NormalY=0 NormalZ=1 AngleXU=0 Radius=1
    g297: Circle CenterX=27.9965 CenterY=107.79 CenterZ=0 NormalX=0 NormalY=0 NormalZ=1 AngleXU=0 Radius=1
    g298: BSplineCurve PolesCount=3 KnotsCount=2 Degree=2 IsPeriodic=0
    g299: GeomPoint X=35.5028 Y=105.865 Z=0
    g300: GeomPoint X=27.9965 Y=107.79 Z=0
    g301: LineSegment StartX=2.07281 StartY=124.221 StartZ=0 EndX=42.0728 EndY=124.221 EndZ=0
    g302: LineSegment StartX=46.0728 StartY=120.221 StartZ=0 EndX=46.0728 EndY=109.865 EndZ=0
    g303: LineSegment StartX=42.0728 StartY=105.865 StartZ=0 EndX=35.5028 EndY=105.865 EndZ=0
    g304: LineSegment StartX=27.9965 StartY=107.79 StartZ=0 EndX=1.57905 EndY=122.295 EndZ=0
    g305: Circle CenterX=42.5666 CenterY=-67.3492 CenterZ=0 NormalX=0 NormalY=0 NormalZ=1 AngleXU=0 Radius=1
    g306: Circle CenterX=46.0728 CenterY=-65.424 CenterZ=0 NormalX=0 NormalY=0 NormalZ=1 AngleXU=0 Radius=1
    g307: Circle CenterX=46.0728 CenterY=-69.424 CenterZ=0 NormalX=0 NormalY=0 NormalZ=1 AngleXU=0 Radius=1
    g308: BSplineCurve PolesCount=3 KnotsCount=2 Degree=2 IsPeriodic=0
    g309: GeomPoint X=42.5666 Y=-67.3492 Z=0
    g310: GeomPoint X=46.0728 Y=-69.424 Z=0
    g311: Circle CenterX=46.0728 CenterY=-87.7794 CenterZ=0 NormalX=0 NormalY=0 NormalZ=1 AngleXU=0 Radius=1
    g312: Circle CenterX=46.0728 CenterY=-91.7794 CenterZ=0 NormalX=0 NormalY=0 NormalZ=1 AngleXU=0 Radius=1
    g313: Circle CenterX=42.0728 CenterY=-91.7794 CenterZ=0 NormalX=0 NormalY=0 NormalZ=1 AngleXU=0 Radius=1
    g314: BSplineCurve PolesCount=3 KnotsCount=2 Degree=2 IsPeriodic=0
    g315: GeomPoint X=46.0728 Y=-87.7794 Z=0
    g316: GeomPoint X=42.0728 Y=-91.7794 Z=0
    g317: Circle CenterX=2.07281 CenterY=-91.7794 CenterZ=0 NormalX=0 NormalY=0 NormalZ=1 AngleXU=0 Radius=1
    g318: Circle CenterX=-1.92719 CenterY=-91.7794 CenterZ=0 NormalX=0 NormalY=0 NormalZ=1 AngleXU=0 Radius=1
    g319: Circle CenterX=1.57905 CenterY=-89.8542 CenterZ=0 NormalX=0 NormalY=0 NormalZ=1 AngleXU=0 Radius=1
    g320: BSplineCurve PolesCount=3 KnotsCount=2 Degree=2 IsPeriodic=0
    g321: GeomPoint X=2.07281 Y=-91.7794 Z=0
    g322: GeomPoint X=1.57905 Y=-89.8542 Z=0
    g323: LineSegment StartX=2.07281 StartY=-91.7794 StartZ=0 EndX=42.0728 EndY=-91.7794 EndZ=0
    g324: LineSegment StartX=46.0728 StartY=-87.7794 StartZ=0 EndX=46.0728 EndY=-69.424 EndZ=0
    g325: LineSegment StartX=42.5666 StartY=-67.3492 StartZ=0 EndX=1.57905 EndY=-89.8542 EndZ=0
    g326: Circle CenterX=322.073 CenterY=76.4095 CenterZ=0 NormalX=0 NormalY=0 NormalZ=1 AngleXU=0 Radius=4
    g327: BSplineCurve PolesCount=3 KnotsCount=2 Degree=2 IsPeriodic=0
    g328: GeomPoint X=318.073 Y=72.4095 Z=0
    g329: GeomPoint X=322.073 Y=76.4095 Z=0
    g330: Circle CenterX=375.073 CenterY=72.4095 CenterZ=0 NormalX=0 NormalY=0 NormalZ=1 AngleXU=0 Radius=1
    g331: Circle CenterX=375.073 CenterY=76.4095 CenterZ=0 NormalX=0 NormalY=0 NormalZ=1 AngleXU=0 Radius=1
    g332: Circle CenterX=371.073 CenterY=76.4095 CenterZ=0 NormalX=0 NormalY=0 NormalZ=1 AngleXU=0 Radius=1
    g333: BSplineCurve PolesCount=3 KnotsCount=2 Degree=2 IsPeriodic=0
    g334: GeomPoint X=375.073 Y=72.4095 Z=0
    g335: GeomPoint X=371.073 Y=76.4095 Z=0
    g336: LineSegment StartX=322.073 StartY=76.4095 StartZ=0 EndX=371.073 EndY=76.4095 EndZ=0
    g337: LineSegment StartX=318.073 StartY=72.4095 StartZ=0 EndX=318.073 EndY=-47.4805 EndZ=0
    g338: LineSegment StartX=375.073 StartY=72.4095 StartZ=0 EndX=375.073 EndY=-78.7896 EndZ=0
    g339: ArcOfCircle CenterX=-26.9272 CenterY=22.1087 CenterZ=0 NormalX=0 NormalY=0 NormalZ=1 AngleXU=0 Radius=4 StartAngle=5e-16 EndAngle=3.14159
    g340: LineSegment StartX=-22.9272 StartY=22.1087 StartZ=0 EndX=-18.9272 EndY=-83.7794 EndZ=0
    g341: LineSegment StartX=-34.9272 StartY=-83.7794 StartZ=0 EndX=-30.9272 EndY=22.1087 EndZ=0
    g342: ArcOfCircle CenterX=391.073 CenterY=22.1087 CenterZ=0 NormalX=0 NormalY=0 NormalZ=1 AngleXU=0 Radius=4 StartAngle=0 EndAngle=3.14159
    g343: LineSegment StartX=387.073 StartY=22.1087 StartZ=0 EndX=383.073 EndY=-83.7794 EndZ=0
    g344: LineSegment StartX=395.073 StartY=22.1087 StartZ=0 EndX=399.073 EndY=-83.7794 EndZ=0
    g345: Circle CenterX=-10.9272 CenterY=-78.7794 CenterZ=0 NormalX=0 NormalY=0 NormalZ=1 AngleXU=0 Radius=1
    g346: Circle CenterX=-10.9272 CenterY=-82.7794 CenterZ=0 NormalX=0 NormalY=0 NormalZ=1 AngleXU=0 Radius=1
    g347: Circle CenterX=-7.42095 CenterY=-80.8542 CenterZ=0 NormalX=0 NormalY=0 NormalZ=1 AngleXU=0 Radius=1
    g348: BSplineCurve PolesCount=3 KnotsCount=2 Degree=2 IsPeriodic=0
    g349: GeomPoint X=-10.9272 Y=-78.7794 Z=0
    g350: GeomPoint X=-7.42095 Y=-80.8542 Z=0
    g351: Circle CenterX=42.5666 CenterY=-53.4075 CenterZ=0 NormalX=0 NormalY=0 NormalZ=1 AngleXU=0 Radius=1
    g352: Circle CenterX=46.0728 CenterY=-51.4823 CenterZ=0 NormalX=0 NormalY=0 NormalZ=1 AngleXU=0 Radius=1
    g353: Circle CenterX=46.0728 CenterY=-47.4823 CenterZ=0 NormalX=0 NormalY=0 NormalZ=1 AngleXU=0 Radius=1
    g354: BSplineCurve PolesCount=3 KnotsCount=2 Degree=2 IsPeriodic=0
    g355: GeomPoint X=42.5666 Y=-53.4075 Z=0
    g356: GeomPoint X=46.0728 Y=-47.4823 Z=0
    g357: Circle CenterX=46.0728 CenterY=72.4095 CenterZ=0 NormalX=0 NormalY=0 NormalZ=1 AngleXU=0 Radius=1
    g358: Circle CenterX=46.0728 CenterY=76.4095 CenterZ=0 NormalX=0 NormalY=0 NormalZ=1 AngleXU=0 Radius=1
    g359: Circle CenterX=42.0728 CenterY=76.4095 CenterZ=0 NormalX=0 NormalY=0 NormalZ=1 AngleXU=0 Radius=1
    g360: BSplineCurve PolesCount=3 KnotsCount=2 Degree=2 IsPeriodic=0
    g361: GeomPoint X=46.0728 Y=72.4095 Z=0
    g362: GeomPoint X=42.0728 Y=76.4095 Z=0
    g363: Circle CenterX=-6.92718 CenterY=76.4095 CenterZ=0 NormalX=0 NormalY=0 NormalZ=1 AngleXU=0 Radius=1
    g364: Circle CenterX=-10.9272 CenterY=76.4095 CenterZ=0 NormalX=0 NormalY=0 NormalZ=1 AngleXU=0 Radius=1
    g365: Circle CenterX=-10.9272 CenterY=72.4095 CenterZ=0 NormalX=0 NormalY=0 NormalZ=1 AngleXU=0 Radius=1
    g366: BSplineCurve PolesCount=3 KnotsCount=2 Degree=2 IsPeriodic=0
    g367: GeomPoint X=-6.92718 Y=76.4095 Z=0
    g368: GeomPoint X=-10.9272 Y=72.4095 Z=0
  constraints (602):
    c: Vertical(g0)
    c: Vertical(g1)
    c: Block(g1)
    c: Block(g0)
    c: Weight(g4) = 1
    c: Equal(g4,g5)
    c: Equal(g4,g6)
    c: InternalAlignment(g4,g7)
    c: InternalAlignment(g5,g7)
    c: InternalAlignment(g6,g7)
    c: InternalAlignment(g8,g7)
    c: InternalAlignment(g9,g7)
    c: Weight(g10) = 1
    c: Equal(g10,g11)
    c: Equal(g10,g12)
    c: InternalAlignment(g10,g13)
    c: InternalAlignment(g11,g13)
    c: InternalAlignment(g12,g13)
    c: InternalAlignment(g14,g13)
    c: InternalAlignment(g15,g13)
    c: Block(g13)
    c: Block(g7)
    c: Weight(g16) = 1
    c: Equal(g16,g17)
    c: Equal(g16,g18)
    c: InternalAlignment(g16,g19)
    c: InternalAlignment(g17,g19)
    c: InternalAlignment(g18,g19)
    c: InternalAlignment(g20,g19)
    c: InternalAlignment(g21,g19)
    c: Weight(g22) = 1
    c: Equal(g22,g23)
    c: Equal(g22,g24)
    c: InternalAlignment(g22,g25)
    c: InternalAlignment(g23,g25)
    c: InternalAlignment(g24,g25)
    c: InternalAlignment(g26,g25)
    c: InternalAlignment(g27,g25)
    c: Block(g25)
    c: Block(g19)
    c: Weight(g28) = 1
    c: Equal(g28,g29)
    c: Equal(g28,g30)
    c: InternalAlignment(g28,g31)
    c: InternalAlignment(g29,g31)
    c: InternalAlignment(g30,g31)
    c: InternalAlignment(g32,g31)
    c: InternalAlignment(g33,g31)
    c: Weight(g34) = 1
    c: Equal(g34,g35)
    c: Equal(g34,g36)
    c: InternalAlignment(g34,g37)
    c: InternalAlignment(g35,g37)
    c: InternalAlignment(g36,g37)
    c: InternalAlignment(g38,g37)
    c: InternalAlignment(g39,g37)
    c: Block(g31)
    c: Block(g37)
    c: Coincident(g40,g1)
    c: Coincident(g40,g0)
    c: Horizontal(g40)
    c: Distance(g40) = 450
    c: Coincident(g41,g1)
    c: Coincident(g41,g0)
    c: Horizontal(g41)
    c: Weight(g42) = 1
    c: Equal(g42,g43)
    c: Equal(g42,g44)
    c: InternalAlignment(g42,g45)
    c: InternalAlignment(g43,g45)
    c: InternalAlignment(g44,g45)
    c: InternalAlignment(g46,g45)
    c: InternalAlignment(g47,g45)
    c: Block(g45)
    c: Weight(g48) = 1
    c: Equal(g48,g49)
    c: Equal(g48,g50)
    c: InternalAlignment(g48,g51)
    c: InternalAlignment(g49,g51)
    c: InternalAlignment(g50,g51)
    c: InternalAlignment(g52,g51)
    c: InternalAlignment(g53,g51)
    c: Block(g51)
    c: Weight(g54) = 1
    c: Equal(g54,g55)
    c: Equal(g54,g56)
    c: InternalAlignment(g54,g57)
    c: InternalAlignment(g55,g57)
    c: InternalAlignment(g56,g57)
    c: InternalAlignment(g58,g57)
    c: InternalAlignment(g59,g57)
    c: Block(g57)
    c: Weight(g60) = 1
    c: Equal(g60,g61)
    c: Equal(g60,g62)
    c: InternalAlignment(g60,g63)
    c: InternalAlignment(g61,g63)
    c: InternalAlignment(g62,g63)
    c: InternalAlignment(g64,g63)
    c: InternalAlignment(g65,g63)
    c: Block(g63)
    c: Weight(g66) = 1
    c: Equal(g66,g67)
    c: Equal(g66,g68)
    c: InternalAlignment(g66,g69)
    c: InternalAlignment(g67,g69)
    c: InternalAlignment(g68,g69)
    c: InternalAlignment(g70,g69)
    c: InternalAlignment(g71,g69)
    c: Weight(g72) = 1
    c: Equal(g72,g73)
    c: Equal(g72,g74)
    c: InternalAlignment(g72,g75)
    c: InternalAlignment(g73,g75)
    c: InternalAlignment(g74,g75)
    c: InternalAlignment(g76,g75)
    c: InternalAlignment(g77,g75)
    c: Block(g69)
    c: Block(g75)
    c: Coincident(g78,g69)
    c: Coincident(g78,g75)
    c: Vertical(g78)
    c: Coincident(g79,g69)
    c: Coincident(g79,g51)
    c: Coincident(g80,g51)
    c: Coincident(g80,g75)
    c: Weight(g81) = 1
    c: Equal(g81,g82)
    c: Equal(g81,g83)
    c: InternalAlignment(g81,g84)
    c: InternalAlignment(g82,g84)
    c: InternalAlignment(g83,g84)
    c: InternalAlignment(g85,g84)
    c: InternalAlignment(g86,g84)
    c: Weight(g87) = 1
    c: Equal(g87,g88)
    c: Equal(g87,g89)
    c: InternalAlignment(g87,g90)
    c: InternalAlignment(g88,g90)
    c: InternalAlignment(g89,g90)
    c: InternalAlignment(g91,g90)
    c: InternalAlignment(g92,g90)
    c: Block(g84)
    c: Block(g90)
    c: Coincident(g93,g84)
    c: Coincident(g93,g90)
    c: Vertical(g93)
    c: Coincident(g94,g84)
    c: Coincident(g94,g45)
    c: Coincident(g95,g45)
    c: Coincident(g95,g90)
    c: Weight(g96) = 1
    c: Equal(g96,g97)
    c: Equal(g96,g98)
    c: InternalAlignment(g96,g99)
    c: InternalAlignment(g97,g99)
    c: InternalAlignment(g98,g99)
    c: InternalAlignment(g100,g99)
    c: InternalAlignment(g101,g99)
    c: Weight(g102) = 1
    c: Equal(g102,g103)
    c: Equal(g102,g104)
    c: InternalAlignment(g102,g105)
    c: InternalAlignment(g103,g105)
    c: InternalAlignment(g104,g105)
    c: InternalAlignment(g106,g105)
    c: InternalAlignment(g107,g105)
    c: Block(g99)
    c: Block(g105)
    c: Coincident(g108,g99)
    c: Coincident(g108,g105)
    c: Vertical(g108)
    c: Coincident(g109,g105)
    c: Coincident(g109,g63)
    c: Coincident(g110,g63)
    c: Coincident(g110,g99)
    c: Weight(g111) = 1
    c: Equal(g111,g112)
    c: Equal(g111,g113)
    c: InternalAlignment(g111,g114)
    c: InternalAlignment(g112,g114)
    c: InternalAlignment(g113,g114)
    c: InternalAlignment(g115,g114)
    c: InternalAlignment(g116,g114)
    c: Weight(g117) = 1
    c: Equal(g117,g118)
    c: Equal(g117,g119)
    c: InternalAlignment(g117,g120)
    c: InternalAlignment(g118,g120)
    c: InternalAlignment(g119,g120)
    c: InternalAlignment(g121,g120)
    c: InternalAlignment(g122,g120)
    c: Block(g114)
    c: Block(g120)
    c: Coincident(g123,g114)
    c: Coincident(g123,g120)
    c: Vertical(g123)
    c: Coincident(g124,g120)
    c: Coincident(g124,g57)
    c: Coincident(g125,g57)
    c: Coincident(g125,g114)
    c: Weight(g126) = 1
    c: Equal(g126,g127)
    c: Equal(g126,g128)
    c: InternalAlignment(g126,g129)
    c: InternalAlignment(g127,g129)
    c: InternalAlignment(g128,g129)
    c: InternalAlignment(g130,g129)
    c: InternalAlignment(g131,g129)
    c: Weight(g132) = 1
    c: Equal(g132,g133)
    c: Equal(g132,g134)
    c: InternalAlignment(g132,g135)
    c: InternalAlignment(g133,g135)
    c: InternalAlignment(g134,g135)
    c: InternalAlignment(g136,g135)
    c: InternalAlignment(g137,g135)
    c: Weight(g138) = 1
    c: Equal(g138,g139)
    c: Equal(g138,g140)
    c: InternalAlignment(g138,g141)
    c: InternalAlignment(g139,g141)
    c: InternalAlignment(g140,g141)
    c: InternalAlignment(g142,g141)
    c: InternalAlignment(g143,g141)
    c: Weight(g144) = 1
    c: Equal(g144,g145)
    c: Equal(g144,g146)
    c: InternalAlignment(g144,g147)
    c: InternalAlignment(g145,g147)
    c: InternalAlignment(g146,g147)
    c: InternalAlignment(g148,g147)
    c: InternalAlignment(g149,g147)
    c: Block(g147)
    c: Block(g141)
    c: Block(g135)
    c: Block(g129)
    c: Coincident(g150,g25)
    c: Coincident(g150,g147)
    c: Coincident(g151,g147)
    c: Coincident(g151,g141)
    c: Horizontal(g151)
    c: Coincident(g152,g141)
    c: Coincident(g152,g25)
    c: Vertical(g152)
    c: Coincident(g153,g19)
    c: Coincident(g153,g135)
    c: Vertical(g153)
    c: Coincident(g154,g135)
    c: Coincident(g154,g129)
    c: Horizontal(g154)
    c: Coincident(g155,g129)
    c: Coincident(g155,g19)
    c: Weight(g156) = 1
    c: Equal(g156,g157)
    c: Equal(g156,g158)
    c: InternalAlignment(g156,g159)
    c: InternalAlignment(g157,g159)
    c: InternalAlignment(g158,g159)
    c: InternalAlignment(g160,g159)
    c: InternalAlignment(g161,g159)
    c: Weight(g162) = 1
    c: Equal(g162,g163)
    c: Equal(g162,g164)
    c: InternalAlignment(g162,g165)
    c: InternalAlignment(g163,g165)
    c: InternalAlignment(g164,g165)
    c: InternalAlignment(g166,g165)
    c: InternalAlignment(g167,g165)
    c: Weight(g168) = 1
    c: Equal(g168,g169)
    c: Equal(g168,g170)
    c: InternalAlignment(g168,g171)
    c: InternalAlignment(g169,g171)
    c: InternalAlignment(g170,g171)
    c: InternalAlignment(g172,g171)
    c: InternalAlignment(g173,g171)
    c: Weight(g174) = 1
    c: Equal(g174,g175)
    c: Equal(g174,g176)
    c: InternalAlignment(g174,g177)
    c: InternalAlignment(g175,g177)
    c: InternalAlignment(g176,g177)
    c: InternalAlignment(g178,g177)
    c: InternalAlignment(g179,g177)
    c: Block(g177)
    c: Block(g171)
    c: Block(g165)
    c: Block(g159)
    c: Coincident(g180,g177)
    c: Coincident(g180,g171)
    c: Horizontal(g180)
    c: Coincident(g181,g171)
    c: Coincident(g181,g7)
    c: Vertical(g181)
    c: Coincident(g182,g13)
    c: Coincident(g182,g165)
    c: Vertical(g182)
    c: Coincident(g183,g165)
    c: Coincident(g183,g159)
    c: Horizontal(g183)
    c: Coincident(g184,g159)
    c: Coincident(g184,g13)
    c: Coincident(g185,g7)
    c: Weight(g186) = 1
    c: Equal(g186,g187)
    c: Equal(g186,g188)
    c: InternalAlignment(g186,g189)
    c: InternalAlignment(g187,g189)
    c: InternalAlignment(g188,g189)
    c: InternalAlignment(g190,g189)
    c: InternalAlignment(g191,g189)
    c: Weight(g192) = 1
    c: Equal(g192,g193)
    c: Equal(g192,g194)
    c: InternalAlignment(g192,g195)
    c: InternalAlignment(g193,g195)
    c: InternalAlignment(g194,g195)
    c: InternalAlignment(g196,g195)
    c: InternalAlignment(g197,g195)
    c: Block(g195)
    c: Block(g189)
    c: Coincident(g198,g195)
    c: Coincident(g198,g31)
    c: Coincident(g199,g31)
    c: Coincident(g199,g189)
    c: Coincident(g200,g189)
    c: Coincident(g200,g195)
    c: Vertical(g200)
    c: Weight(g201) = 1
    c: Equal(g201,g202)
    c: Equal(g201,g203)
    c: InternalAlignment(g201,g204)
    c: InternalAlignment(g202,g204)
    c: InternalAlignment(g203,g204)
    c: InternalAlignment(g205,g204)
    c: InternalAlignment(g206,g204)
    c: Weight(g207) = 1
    c: Equal(g207,g208)
    c: Equal(g207,g209)
    c: InternalAlignment(g207,g210)
    c: InternalAlignment(g208,g210)
    c: InternalAlignment(g209,g210)
    c: InternalAlignment(g211,g210)
    c: InternalAlignment(g212,g210)
    c: Block(g210)
    c: Block(g204)
    c: Coincident(g213,g204)
    c: Coincident(g213,g37)
    c: Coincident(g214,g37)
    c: Coincident(g214,g210)
    c: Coincident(g215,g210)
    c: Coincident(g215,g204)
    c: Vertical(g215)
    c: Horizontal(g216)
    c: Block(g216)
    c: Vertical(g217)
    c: Block(g217)
    c: Block(g218)
    c: Weight(g219) = 1
    c: Equal(g219,g220)
    c: Equal(g219,g221)
    c: InternalAlignment(g219,g222)
    c: InternalAlignment(g220,g222)
    c: InternalAlignment(g221,g222)
    c: InternalAlignment(g223,g222)
    c: InternalAlignment(g224,g222)
    c: Weight(g225) = 1
    c: Equal(g225,g226)
    c: Equal(g225,g227)
    c: InternalAlignment(g225,g228)
    c: InternalAlignment(g226,g228)
    c: InternalAlignment(g227,g228)
    c: InternalAlignment(g229,g228)
    c: InternalAlignment(g230,g228)
    c: Weight(g231) = 1
    c: Equal(g231,g232)
    c: Equal(g231,g233)
    c: InternalAlignment(g231,g234)
    c: InternalAlignment(g232,g234)
    c: InternalAlignment(g233,g234)
    c: InternalAlignment(g235,g234)
    c: InternalAlignment(g236,g234)
    c: Weight(g237) = 1
    c: Equal(g237,g238)
    c: Equal(g237,g239)
    c: InternalAlignment(g237,g240)
    c: InternalAlignment(g238,g240)
    c: InternalAlignment(g239,g240)
    c: InternalAlignment(g241,g240)
    c: InternalAlignment(g242,g240)
    c: Block(g222)
    c: Block(g228)
    c: Block(g234)
    c: Block(g240)
    c: Coincident(g243,g228)
    c: Coincident(g243,g222)
    c: Horizontal(g243)
    c: Block(g185)
    c: Weight(g244) = 1
    c: Equal(g244,g245)
    c: Equal(g244,g246)
    c: InternalAlignment(g244,g247)
    c: InternalAlignment(g245,g247)
    c: InternalAlignment(g246,g247)
    c: InternalAlignment(g248,g247)
    c: InternalAlignment(g249,g247)
    c: Weight(g250) = 1
    c: Equal(g250,g251)
    c: Equal(g250,g252)
    c: InternalAlignment(g250,g253)
    c: InternalAlignment(g251,g253)
    c: InternalAlignment(g252,g253)
    c: InternalAlignment(g254,g253)
    c: InternalAlignment(g255,g253)
    c: Block(g247)
    c: Block(g253)
    c: Coincident(g256,g247)
    c: Coincident(g256,g253)
    c: Weight(g257) = 1
    c: Equal(g257,g258)
    c: Equal(g257,g259)
    c: InternalAlignment(g257,g260)
    c: InternalAlignment(g258,g260)
    c: InternalAlignment(g259,g260)
    c: InternalAlignment(g261,g260)
    c: InternalAlignment(g262,g260)
    c: Weight(g263) = 1
    c: Equal(g263,g264)
    c: Equal(g263,g265)
    c: InternalAlignment(g263,g266)
    c: InternalAlignment(g264,g266)
    c: InternalAlignment(g265,g266)
    c: InternalAlignment(g267,g266)
    c: InternalAlignment(g268,g266)
    c: Weight(g269) = 1
    c: Equal(g269,g270)
    c: Equal(g269,g271)
    c: InternalAlignment(g269,g272)
    c: InternalAlignment(g270,g272)
    c: InternalAlignment(g271,g272)
    c: InternalAlignment(g273,g272)
    c: InternalAlignment(g274,g272)
    c: Block(g272)
    c: Block(g266)
    c: Block(g260)
    c: Coincident(g275,g266)
    c: Coincident(g275,g260)
    c: Coincident(g276,g260)
    c: Coincident(g276,g272)
    c: Vertical(g276)
    c: Coincident(g277,g272)
    c: Coincident(g277,g266)
    c: Horizontal(g277)
    c: Weight(g278) = 1
    c: Equal(g278,g279)
    c: InternalAlignment(g278,g280)
    c: InternalAlignment(g279,g280)
    c: InternalAlignment(g281,g280)
    c: InternalAlignment(g282,g280)
    c: Weight(g283) = 1
    c: InternalAlignment(g284,g286)
    c: InternalAlignment(g285,g286)
    c: InternalAlignment(g287,g286)
    c: InternalAlignment(g288,g286)
    c: Weight(g289) = 1
    c: Equal(g289,g290)
    c: Equal(g289,g291)
    c: InternalAlignment(g289,g292)
    c: InternalAlignment(g290,g292)
    c: InternalAlignment(g291,g292)
    c: InternalAlignment(g293,g292)
    c: InternalAlignment(g294,g292)
    c: Equal(g295,g296)
    c: Equal(g295,g297)
    c: InternalAlignment(g295,g298)
    c: InternalAlignment(g296,g298)
    c: InternalAlignment(g297,g298)
    c: InternalAlignment(g299,g298)
    c: InternalAlignment(g300,g298)
    c: Block(g286)
    c: Block(g292)
    c: Block(g298)
    c: Block(g280)
    c: Coincident(g301,g280)
    c: Coincident(g301,g286)
    c: Horizontal(g301)
    c: Coincident(g302,g286)
    c: Coincident(g302,g292)
    c: Vertical(g302)
    c: Coincident(g303,g292)
    c: Coincident(g303,g298)
    c: Horizontal(g303)
    c: Coincident(g304,g298)
    c: Coincident(g304,g280)
    c: Weight(g305) = 1
    c: Equal(g305,g306)
    c: Equal(g305,g307)
    c: InternalAlignment(g305,g308)
    c: InternalAlignment(g306,g308)
    c: InternalAlignment(g307,g308)
    c: InternalAlignment(g309,g308)
    c: InternalAlignment(g310,g308)
    c: Weight(g311) = 1
    c: Equal(g311,g312)
    c: Equal(g311,g313)
    c: InternalAlignment(g311,g314)
    c: InternalAlignment(g312,g314)
    c: InternalAlignment(g313,g314)
    c: InternalAlignment(g315,g314)
    c: InternalAlignment(g316,g314)
    c: Weight(g317) = 1
    c: Equal(g317,g318)
    c: Equal(g317,g319)
    c: InternalAlignment(g317,g320)
    c: InternalAlignment(g318,g320)
    c: InternalAlignment(g319,g320)
    c: InternalAlignment(g321,g320)
    c: InternalAlignment(g322,g320)
    c: Block(g320)
    c: Block(g314)
    c: Block(g308)
    c: Coincident(g323,g320)
    c: Coincident(g323,g314)
    c: Horizontal(g323)
    c: Coincident(g324,g314)
    c: Coincident(g324,g308)
    c: Vertical(g324)
    c: Coincident(g325,g308)
    c: Coincident(g325,g320)
    c: InternalAlignment(g326,g327)
    c: InternalAlignment(g328,g327)
    c: InternalAlignment(g329,g327)
    c: Block(g327)
    c: Equal(g330,g331)
    c: Equal(g330,g332)
    c: InternalAlignment(g330,g333)
    c: InternalAlignment(g331,g333)
    c: InternalAlignment(g332,g333)
    c: InternalAlignment(g334,g333)
    c: InternalAlignment(g335,g333)
    c: Block(g333)
    c: Coincident(g336,g327)
    c: Horizontal(g336)
    c: Block(g336)
    c: Coincident(g337,g327)
    c: Coincident(g337,g253)
    c: Vertical(g337)
    c: Coincident(g338,g333)
    c: Coincident(g338,g247)
    c: Vertical(g338)
    c: Block(g339)
    c: Block(g2)
    c: Distance(g337) = 119.89
    c: Coincident(g340,g339)
    c: Coincident(g340,g2)
    c: Coincident(g341,g2)
    c: Coincident(g341,g339)
    c: Block(g3)
    c: Block(g342)
    c: Coincident(g343,g342)
    c: Coincident(g343,g3)
    c: Coincident(g344,g342)
    c: Coincident(g344,g3)
    c: Block(g344)
    c: Block(g343)
    c: Weight(g345) = 1
    c: Equal(g345,g346)
    c: Equal(g345,g347)
    c: InternalAlignment(g345,g348)
    c: InternalAlignment(g346,g348)
    c: InternalAlignment(g347,g348)
    c: InternalAlignment(g349,g348)
    c: InternalAlignment(g350,g348)
    c: Weight(g351) = 1
    c: Equal(g351,g352)
    c: Equal(g351,g353)
    c: InternalAlignment(g351,g354)
    c: InternalAlignment(g352,g354)
    c: InternalAlignment(g353,g354)
    c: InternalAlignment(g355,g354)
    c: InternalAlignment(g356,g354)
    c: Weight(g357) = 1
    c: Equal(g357,g358)
    c: Equal(g357,g359)
    c: InternalAlignment(g357,g360)
    c: InternalAlignment(g358,g360)
    c: InternalAlignment(g359,g360)
    c: InternalAlignment(g361,g360)
    c: InternalAlignment(g362,g360)
    c: Weight(g363) = 1
    c: Equal(g363,g364)
    c: Equal(g363,g365)
    c: InternalAlignment(g363,g366)
    c: InternalAlignment(g364,g366)
    c: InternalAlignment(g365,g366)
    c: InternalAlignment(g367,g366)
    c: InternalAlignment(g368,g366)
    c: Block(g366)
    c: Block(g360)
    c: Block(g354)
    c: Block(g348)
